FCSTD DOCUMENT  (FreeCAD 1.0R39109 (Git))
Label: sway_platform
License: All rights reserved
LicenseURL: https://en.wikipedia.org/wiki/All_rights_reserved
objects: App::Link×28, App::FeaturePython×28, Assembly::JointGroup×1, Assembly::AssemblyObject×1
EXTERNAL_REF file=../parts_library/SC25UU_to_SH25.FCStd obj=Body
EXTERNAL_REF file=../parts_library/SC25UU.FCStd obj=Part__Feature341
EXTERNAL_REF file=../parts_library/SH25.FCStd obj=Part__Feature337
EXTERNAL_REF file=../parts_library/linear_shaft.FCStd obj=Body001
EXTERNAL_REF file=../parts_library/DSG16H_to_SH25.FCStd obj=Body
EXTERNAL_REF file=../parts_library/SFU1605.FCStd obj=Part__Feature048
EXTERNAL_REF file=../parts_library/SFU1605.FCStd obj=Part__Feature047
EXTERNAL_REF file=../parts_library/motor.FCStd obj=SERVOMOTOR_80ST_M02430
EXTERNAL_REF file=../parts_library/coupler.FCStd obj=Body
EXTERNAL_REF file=../parts_library/SFU1605.FCStd obj=SFU1605_250_v6
EXTERNAL_REF file=../parts_library/SFU1605.FCStd obj=BK12_v3
EXTERNAL_REF file=sway_SC25UU_to_SH25_with_plate.FCStd obj=Body
EXTERNAL_REF file=sway_motor_mount_rear_plate.FCStd obj=Body
EXTERNAL_REF file=sway_motor_mount_front_plate.FCStd obj=Body
EXTERNAL_REF file=sway_motor_mount_front_plate_shaft_support.FCStd obj=Body
EXTERNAL_REF file=sway_motor_mount_side.FCStd obj=Body
EXTERNAL_REF file=sway_motor_mount_top.FCStd obj=Body
EXTERNAL_REF file=sway_motor_mount_bottom.FCStd obj=Body

FEATURE [App::Link] SC25UU_to_SH25  label="SC25UU_to_SH25_000"
  LinkedObject = -> <external ../parts_library/SC25UU_to_SH25.FCStd>#Body
FEATURE [App::Link] SC25UU_to_SH026  label="SC25UU_to_SH25_001"
  LinkPlacement = pos=(1e-15,204,-1e-16) rot=(0,0,1;0rad)
  LinkedObject = -> <external ../parts_library/SC25UU_to_SH25.FCStd>#Body
  Placement = pos=(1e-15,204,-1e-16) rot=(0,0,1;0rad)
FEATURE [App::FeaturePython] GroundedJoint  label="GroundedJoint_SC25UU_to_SH25_000"  # Assembly grounded joint (typed FeaturePython)
  ObjectToGround = -> SC25UU_to_SH25
FEATURE [App::FeaturePython] Joint  label="Fixed_SC25UU_to_SH25_001"  # Assembly joint (typed FeaturePython)
  Activated = true
  AngleMax = 0
  AngleMin = 0
  Detach1 = false
  Detach2 = false
  Distance = 0
  Distance2 = 0
  EnableAngleMax = false
  EnableAngleMin = false
  EnableLengthMax = false
  EnableLengthMin = false
  JointType = 0 (Fixed)
  LengthMax = 0
  LengthMin = 0
  Offset2 = pos=(0,0,-204) rot=(0,0,1;0rad)
  Placement1 = pos=(38,-1.5,5) rot=(-1,0,0;1.5708rad)
  Placement2 = pos=(38,-205.5,5) rot=(-1,0,0;1.5708rad)
  Reference1 = -> Assembly [SC25UU_to_SH25.Face9,SC25UU_to_SH25.Face9]
  Reference2 = -> Assembly [SC25UU_to_SH026.Face9,SC25UU_to_SH026.Face9]
FEATURE [App::Link] SC25UU  label="SC25UU_000"
  LinkPlacement = pos=(38,67,-415.5) rot=(1,0,0;1.5708rad)
  LinkedObject = -> <external ../parts_library/SC25UU.FCStd>#Part__Feature341
  Placement = pos=(38,67,-415.5) rot=(1,0,0;1.5708rad)
FEATURE [App::Link] SC25UU001  label="SC25UU_001"
  LinkPlacement = pos=(38,271,-415.5) rot=(1,0,0;1.5708rad)
  LinkedObject = -> <external ../parts_library/SC25UU.FCStd>#Part__Feature341
  Placement = pos=(38,271,-415.5) rot=(1,0,0;1.5708rad)
FEATURE [App::Link] SC25UU002  label="SC25UU_002"
  LinkPlacement = pos=(442,67,-415.5) rot=(1,0,0;1.5708rad)
  LinkedObject = -> <external ../parts_library/SC25UU.FCStd>#Part__Feature341
  Placement = pos=(442,67,-415.5) rot=(1,0,0;1.5708rad)
FEATURE [App::Link] SC25UU003  label="SC25UU_003"
  LinkPlacement = pos=(442,271,-415.5) rot=(1,0,0;1.5708rad)
  LinkedObject = -> <external ../parts_library/SC25UU.FCStd>#Part__Feature341
  Placement = pos=(442,271,-415.5) rot=(1,0,0;1.5708rad)
FEATURE [App::FeaturePython] Joint003  label="Fixed_SC25UU_000"  # Assembly joint (typed FeaturePython)
  Activated = true
  AngleMax = 0
  AngleMin = 0
  Detach1 = false
  Detach2 = false
  Distance = 0
  Distance2 = 0
  EnableAngleMax = false
  EnableAngleMin = false
  EnableLengthMax = false
  EnableLengthMin = false
  JointType = 0 (Fixed)
  LengthMax = 0
  LengthMin = 0
  Offset2 = pos=(0,0,0) rot=(0,0,-1;1.5708rad)
  Placement1 = pos=(-27,415.5,58.5) rot=(0.57735,-0.57735,0.57735;2.0944rad)
  Placement2 = pos=(11,8.5,0) rot=(0,0,-1;1.5708rad)
  Reference1 = -> Assembly [SC25UU.Edge66,SC25UU.Edge66]
  Reference2 = -> Assembly [SC25UU_to_SH25.Edge16,SC25UU_to_SH25.Edge16]
FEATURE [App::FeaturePython] Joint004  label="Fixed_SC25UU_001"  # Assembly joint (typed FeaturePython)
  Activated = true
  AngleMax = 0
  AngleMin = 0
  Detach1 = false
  Detach2 = false
  Distance = 0
  Distance2 = 0
  EnableAngleMax = false
  EnableAngleMin = false
  EnableLengthMax = false
  EnableLengthMin = false
  JointType = 0 (Fixed)
  LengthMax = 0
  LengthMin = 0
  Offset2 = pos=(0,0,0) rot=(0,0,-1;1.5708rad)
  Placement1 = pos=(11,8.5,0) rot=(0,0,1;0rad)
  Placement2 = pos=(-27,415.5,58.5) rot=(1,0,0;1.5708rad)
  Reference1 = -> Assembly [SC25UU_to_SH026.Edge16,SC25UU_to_SH026.Edge16]
  Reference2 = -> Assembly [SC25UU001.Edge66,SC25UU001.Edge66]
FEATURE [App::Link] SH25  label="SH25_000"
  LinkPlacement = pos=(-901.062,343.027,-226.938) rot=(0,0,1;0rad)
  LinkedObject = -> <external ../parts_library/SH25.FCStd>#Part__Feature337
  Placement = pos=(-901.062,343.027,-226.938) rot=(0,0,1;0rad)
FEATURE [App::Link] SH026  label="SH25_001"
  LinkPlacement = pos=(977.062,-72.0272,-226.938) rot=(0,0,1;3.14159rad)
  LinkedObject = -> <external ../parts_library/SH25.FCStd>#Part__Feature337
  Placement = pos=(977.062,-72.0272,-226.938) rot=(0,0,1;3.14159rad)
FEATURE [App::Link] SH027  label="SH25_002"
  LinkPlacement = pos=(-497.062,343.027,-226.938) rot=(0,0,1;0rad)
  LinkedObject = -> <external ../parts_library/SH25.FCStd>#Part__Feature337
  Placement = pos=(-497.062,343.027,-226.938) rot=(0,0,1;0rad)
FEATURE [App::Link] SH028  label="SH25_003"
  LinkPlacement = pos=(1381.06,-72.0272,-226.938) rot=(0,0,1;3.14159rad)
  LinkedObject = -> <external ../parts_library/SH25.FCStd>#Part__Feature337
  Placement = pos=(1381.06,-72.0272,-226.938) rot=(0,0,1;3.14159rad)
FEATURE [App::FeaturePython] Joint007  label="Fixed_SH25_000"  # Assembly joint (typed FeaturePython)
  Activated = true
  AngleMax = 0
  AngleMin = 0
  Detach1 = false
  Detach2 = false
  Distance = 0
  Distance2 = 0
  EnableAngleMax = false
  EnableAngleMin = false
  EnableLengthMax = false
  EnableLengthMin = false
  JointType = 0 (Fixed)
  LengthMax = 0
  LengthMin = 0
  Offset2 = pos=(0,0,0) rot=(0,0,1;3.14159rad)
  Placement1 = pos=(38,5.5,10) rot=(0,0,1;0rad)
  Placement2 = pos=(939.062,-337.527,236.938) rot=(0,0,1;0rad)
  Reference1 = -> Assembly [SC25UU_to_SH25.Edge46,SC25UU_to_SH25.Edge46]
  Reference2 = -> Assembly [SH25.Edge16,SH25.Edge16]
FEATURE [App::FeaturePython] Joint008  label="Fixed_SH25_001"  # Assembly joint (typed FeaturePython)
  Activated = true
  AngleMax = 0
  AngleMin = 0
  Detach1 = false
  Detach2 = false
  Distance = 0
  Distance2 = 0
  EnableAngleMax = false
  EnableAngleMin = false
  EnableLengthMax = false
  EnableLengthMin = false
  JointType = 0 (Fixed)
  LengthMax = 0
  LengthMin = 0
  Placement1 = pos=(939.062,-337.527,236.938) rot=(0,0,-1;3.14159rad)
  Placement2 = pos=(38,61.5,10) rot=(0,0,1;0rad)
  Reference1 = -> Assembly [SH026.Edge16,SH026.Edge16]
  Reference2 = -> Assembly [SC25UU_to_SH026.Edge49,SC25UU_to_SH026.Edge49]
FEATURE [App::Link] linear_shaft_25x428  label="linear_shaft_25x428_front"
  LinkPlacement = pos=(454,33.5,45) rot=(0,0,-1;1.5708rad)
  LinkedObject = -> <external ../parts_library/linear_shaft.FCStd>#Body001
  Placement = pos=(454,33.5,45) rot=(0,0,-1;1.5708rad)
FEATURE [App::Link] linear_shaft_25x429  label="linear_shaft_25x428_rear"
  LinkPlacement = pos=(454,237.5,45) rot=(0.707107,0.707107,0;3.14159rad)
  LinkedObject = -> <external ../parts_library/linear_shaft.FCStd>#Body001
  Placement = pos=(454,237.5,45) rot=(0.707107,0.707107,0;3.14159rad)
FEATURE [App::FeaturePython] Joint011  label="Fixed_linear_shaft_25x428_front"  # Assembly joint (typed FeaturePython)
  Activated = true
  AngleMax = 0
  AngleMin = 0
  Detach1 = false
  Detach2 = false
  Distance = 0
  Distance2 = 0
  EnableAngleMax = false
  EnableAngleMin = false
  EnableLengthMax = false
  EnableLengthMin = false
  JointType = 0 (Fixed)
  LengthMax = 0
  LengthMin = 0
  Placement1 = pos=(-7.1e-15,-428,-1.421e-13) rot=(-1,0,0;4.71239rad)
  Placement2 = pos=(927.062,-309.527,271.938) rot=(-0.57735,0.57735,-0.57735;2.0944rad)
  Reference1 = -> Assembly [linear_shaft_25x428.Edge3,linear_shaft_25x428.Edge3]
  Reference2 = -> Assembly [SH25.Edge18,SH25.Edge18]
FEATURE [App::FeaturePython] Joint012  label="Fixed_linear_shaft_25x428_rear"  # Assembly joint (typed FeaturePython)
  Activated = true
  AngleMax = 0
  AngleMin = 0
  Detach1 = false
  Detach2 = false
  Distance = 0
  Distance2 = 0
  EnableAngleMax = false
  EnableAngleMin = false
  EnableLengthMax = false
  EnableLengthMin = false
  JointType = 0 (Fixed)
  LengthMax = 0
  LengthMin = 0
  Placement1 = pos=(0,-428,-1.137e-13) rot=(-1,0,0;4.71239rad)
  Placement2 = pos=(951.062,-309.527,271.938) rot=(-0.57735,0.57735,-0.57735;2.0944rad)
  Reference1 = -> Assembly [linear_shaft_25x429.Edge3,linear_shaft_25x429.Edge3]
  Reference2 = -> Assembly [SH026.Edge26,SH026.Edge26]
FEATURE [App::Link] SH029  label="SH25_004"
  LinkPlacement = pos=(1179.06,-72.0272,-226.938) rot=(0,0,1;3.14159rad)
  LinkedObject = -> <external ../parts_library/SH25.FCStd>#Part__Feature337
  Placement = pos=(1179.06,-72.0272,-226.938) rot=(0,0,1;3.14159rad)
FEATURE [App::FeaturePython] Joint013  label="Fixed_SH25_004"  # Assembly joint (typed FeaturePython)
  Activated = true
  AngleMax = 0
  AngleMin = 0
  Detach1 = false
  Detach2 = false
  Distance = 0
  Distance2 = 0
  EnableAngleMax = false
  EnableAngleMin = false
  EnableLengthMax = false
  EnableLengthMin = false
  JointType = 0 (Fixed)
  LengthMax = 0
  LengthMin = 0
  Offset2 = pos=(0,0,202) rot=(0,0,1;0rad)
  Placement1 = pos=(0,-428,-1.137e-13) rot=(-1,0,0;4.71239rad)
  Placement2 = pos=(1153.06,-309.527,271.938) rot=(-0.57735,0.57735,-0.57735;2.0944rad)
  Reference1 = -> Assembly [linear_shaft_25x429.Edge3,linear_shaft_25x429.Edge3]
  Reference2 = -> Assembly [SH029.Edge26,SH029.Edge26]
FEATURE [App::Link] DSG16H_to_SH25
  LinkPlacement = pos=(215,218.5,-2) rot=(0,0,1;0rad)
  LinkedObject = -> <external ../parts_library/DSG16H_to_SH25.FCStd>#Body
  Placement = pos=(215,218.5,-2) rot=(0,0,1;0rad)
FEATURE [App::FeaturePython] Joint014  label="Fixed_DSG16H_to_SH25"  # Assembly joint (typed FeaturePython)
  Activated = true
  AngleMax = 0
  AngleMin = 0
  Detach1 = false
  Detach2 = false
  Distance = 0
  Distance2 = 0
  EnableAngleMax = false
  EnableAngleMin = false
  EnableLengthMax = false
  EnableLengthMin = false
  JointType = 0 (Fixed)
  LengthMax = 0
  LengthMin = 0
  Placement1 = pos=(25,-9,12) rot=(0,0,1;0rad)
  Placement2 = pos=(939.062,-281.527,236.938) rot=(0,0,-1;3.14159rad)
  Reference1 = -> Assembly [DSG16H_to_SH25.Edge103,DSG16H_to_SH25.Edge103]
  Reference2 = -> Assembly [SH029.Edge8,SH029.Edge8]
FEATURE [App::Link] DSG16H
  LinkPlacement = pos=(240,217.5,-22) rot=(0,0,1;0rad)
  LinkedObject = -> <external ../parts_library/SFU1605.FCStd>#Part__Feature048
  Placement = pos=(240,217.5,-22) rot=(0,0,1;0rad)
FEATURE [App::FeaturePython] Joint015  label="Fixed_DSG16H"  # Assembly joint (typed FeaturePython)
  Activated = true
  AngleMax = 0
  AngleMin = 0
  Detach1 = false
  Detach2 = false
  Distance = 0
  Distance2 = 0
  EnableAngleMax = false
  EnableAngleMin = false
  EnableLengthMax = false
  EnableLengthMin = false
  JointType = 0 (Fixed)
  LengthMax = 0
  LengthMin = 0
  Offset2 = pos=(0,0,0) rot=(0,0,1;3.14159rad)
  Placement1 = pos=(-20,8,20) rot=(0,0,1;3.14159rad)
  Placement2 = pos=(5,7,0) rot=(0,0,1;3.14159rad)
  Reference1 = -> Assembly [DSG16H.Edge1307,DSG16H.Edge1307]
  Reference2 = -> Assembly [DSG16H_to_SH25.Edge20,DSG16H_to_SH25.Edge20]
FEATURE [App::Link] SFU1605_ball_screw_nut
  LinkPlacement = pos=(240,207.25,-22) rot=(0,-1,0;1.5708rad)
  LinkedObject = -> <external ../parts_library/SFU1605.FCStd>#Part__Feature047
  Placement = pos=(240,207.25,-22) rot=(0,-1,0;1.5708rad)
FEATURE [App::FeaturePython] Joint016  label="Fixed_SFU1605_ball_screw_nut"  # Assembly joint (typed FeaturePython)
  Activated = true
  AngleMax = 0
  AngleMin = 0
  Detach1 = false
  Detach2 = false
  Distance = 0
  Distance2 = 0
  EnableAngleMax = false
  EnableAngleMin = false
  EnableLengthMax = false
  EnableLengthMin = false
  JointType = 0 (Fixed)
  LengthMax = 0
  LengthMin = 0
  Placement1 = pos=(0,20,0) rot=(-1,0,0;1.5708rad)
  Placement2 = pos=(7.1e-15,30.25,0) rot=(0.57735,0.57735,-0.57735;2.0944rad)
  Reference1 = -> Assembly [DSG16H.Face478,DSG16H.Face478]
  Reference2 = -> Assembly [SFU1605_ball_screw_nut.Face46,SFU1605_ball_screw_nut.Face46]
FEATURE [App::Link] _0ST_M02438  label="80ST-M02438"
  LinkPlacement = pos=(342.4,135.5,30) rot=(0.57735,-0.57735,-0.57735;2.0944rad)
  LinkedObject = -> <external ../parts_library/motor.FCStd>#SERVOMOTOR_80ST_M02430
  Placement = pos=(342.4,135.5,30) rot=(0.57735,-0.57735,-0.57735;2.0944rad)
FEATURE [App::FeaturePython] Joint017  label="Fixed_80ST-M02438"  # Assembly joint (typed FeaturePython)
  Activated = true
  AngleMax = 0
  AngleMin = 0
  Detach1 = false
  Detach2 = false
  Distance = 0
  Distance2 = 0
  EnableAngleMax = false
  EnableAngleMin = false
  EnableLengthMax = false
  EnableLengthMin = false
  JointType = 0 (Fixed)
  LengthMax = 0
  LengthMin = 0
  Offset1 = pos=(-102,15,0) rot=(0,0,1;0rad)
  Offset2 = pos=(0,0,-31) rot=(0,0,1;0rad)
  Placement1 = pos=(-102,3e-15,15) rot=(-1,0,0;4.71239rad)
  Placement2 = pos=(0,0,-111.6) rot=(0,1,0;3.14159rad)
  Reference1 = -> Assembly [linear_shaft_25x429.Edge2,linear_shaft_25x429.Edge2]
  Reference2 = -> Assembly [_0ST_M02438.Part__Feature004.Edge14,_0ST_M02438.Part__Feature004.Edge14]
FEATURE [App::Link] coupler_10x19
  LinkPlacement = pos=(266.25,135.5,30) rot=(-0.57735,0.57735,0.57735;2.0944rad)
  LinkedObject = -> <external ../parts_library/coupler.FCStd>#Body
  Placement = pos=(266.25,135.5,30) rot=(-0.57735,0.57735,0.57735;2.0944rad)
FEATURE [App::FeaturePython] Joint018  label="Fixed_coupler_10x19"  # Assembly joint (typed FeaturePython)
  Activated = true
  AngleMax = 0
  AngleMin = 0
  Detach1 = false
  Detach2 = false
  Distance = 0
  Distance2 = 0
  EnableAngleMax = false
  EnableAngleMin = false
  EnableLengthMax = false
  EnableLengthMin = false
  JointType = 0 (Fixed)
  LengthMax = 0
  LengthMin = 0
  Offset2 = pos=(0,0,1.65) rot=(0,0,1;0rad)
  Placement1 = pos=(0,0,43) rot=(0,0,1;0rad)
  Placement2 = pos=(3.7e-15,-33.15,-7e-16) rot=(1,0,0;1.5708rad)
  Reference1 = -> Assembly [_0ST_M02438.Part__Feature002.Edge5,_0ST_M02438.Part__Feature002.Edge5]
  Reference2 = -> Assembly [coupler_10x19.Edge9,coupler_10x19.Edge9]
FEATURE [App::Link] SFU1605_ball_screw_250mm
  LinkPlacement = pos=(497.25,135.5,30) rot=(0.57735,0.57735,0.57735;2.0944rad)
  LinkedObject = -> <external ../parts_library/SFU1605.FCStd>#SFU1605_250_v6
  Placement = pos=(497.25,135.5,30) rot=(0.57735,0.57735,0.57735;2.0944rad)
FEATURE [App::FeaturePython] Joint019  label="Fixed_SFU1605_ball_screw_250mm"  # Assembly joint (typed FeaturePython)
  Activated = true
  AngleMax = 0
  AngleMin = 0
  Detach1 = false
  Detach2 = false
  Distance = 0
  Distance2 = 0
  EnableAngleMax = false
  EnableAngleMin = false
  EnableLengthMax = false
  EnableLengthMin = false
  JointType = 0 (Fixed)
  LengthMax = 0
  LengthMin = 0
  Offset2 = pos=(0,0,4) rot=(0,0,1;0rad)
  Placement1 = pos=(2e-16,3e-16,0) rot=(0,0,1;0rad)
  Placement2 = pos=(3.1e-15,-14.5,1.8e-15) rot=(-1,0,0;1.5708rad)
  Reference1 = -> Assembly [SFU1605_ball_screw_250mm.Part__Feature110.Edge105,SFU1605_ball_screw_250mm.Part__Feature110.Edge105]
  Reference2 = -> Assembly [coupler_10x19.Edge7,coupler_10x19.Edge7]
FEATURE [App::Link] BK12
  LinkPlacement = pos=(240,135.5,55) rot=(0.707107,-0.707107,0;3.14159rad)
  LinkedObject = -> <external ../parts_library/SFU1605.FCStd>#BK12_v3
  Placement = pos=(240,135.5,55) rot=(0.707107,-0.707107,0;3.14159rad)
FEATURE [App::FeaturePython] Joint020  label="Fixed_BK12"  # Assembly joint (typed FeaturePython)
  Activated = true
  AngleMax = 0
  AngleMin = 0
  Detach1 = false
  Detach2 = false
  Distance = 0
  Distance2 = 0
  EnableAngleMax = false
  EnableAngleMin = false
  EnableLengthMax = false
  EnableLengthMin = false
  JointType = 0 (Fixed)
  LengthMax = 0
  LengthMin = 0
  Placement1 = pos=(2e-16,3e-16,-53.75) rot=(0,0,1;0rad)
  Placement2 = pos=(1.1e-15,13,25) rot=(0,0.707107,0.707107;3.14159rad)
  Reference1 = -> Assembly [SFU1605_ball_screw_250mm.Part__Feature110.Edge52,SFU1605_ball_screw_250mm.Part__Feature110.Edge52]
  Reference2 = -> Assembly [BK12.Part__Feature030.Edge19,BK12.Part__Feature030.Edge19]
FEATURE [App::Link] sway_SC25UU_to_SH25_with_plate  label="sway_SC25UU_to_SH25_with_plate_001"
  LinkPlacement = pos=(404,204,3e-16) rot=(0,0,1;0rad)
  LinkedObject = -> <external sway_SC25UU_to_SH25_with_plate.FCStd>#Body
  Placement = pos=(404,204,3e-16) rot=(0,0,1;0rad)
FEATURE [App::FeaturePython] Joint022  label="Fixed_SC25UU_003"  # Assembly joint (typed FeaturePython)
  Activated = true
  AngleMax = 0
  AngleMin = 0
  Detach1 = false
  Detach2 = false
  Distance = 0
  Distance2 = 0
  EnableAngleMax = false
  EnableAngleMin = false
  EnableLengthMax = false
  EnableLengthMin = false
  JointType = 0 (Fixed)
  LengthMax = 0
  LengthMin = 0
  Offset2 = pos=(0,0,0) rot=(0,0,-1;1.5708rad)
  Placement1 = pos=(65,58.5,0) rot=(0,0,1;0rad)
  Placement2 = pos=(27,415.5,8.5) rot=(1,0,0;1.5708rad)
  Reference1 = -> Assembly [sway_SC25UU_to_SH25_with_plate.Edge31,sway_SC25UU_to_SH25_with_plate.Edge31]
  Reference2 = -> Assembly [SC25UU003.Edge29,SC25UU003.Edge29]
FEATURE [App::FeaturePython] Joint023  label="Fixed_SH25_003"  # Assembly joint (typed FeaturePython)
  Activated = true
  AngleMax = 0
  AngleMin = 0
  Detach1 = false
  Detach2 = false
  Distance = 0
  Distance2 = 0
  EnableAngleMax = false
  EnableAngleMin = false
  EnableLengthMax = false
  EnableLengthMin = false
  JointType = 0 (Fixed)
  LengthMax = 0
  LengthMin = 0
  Placement1 = pos=(38,61.5,10) rot=(0,0,1;0rad)
  Placement2 = pos=(939.062,-337.527,236.938) rot=(0,0,-1;3.14159rad)
  Reference1 = -> Assembly [sway_SC25UU_to_SH25_with_plate.Edge90,sway_SC25UU_to_SH25_with_plate.Edge90]
  Reference2 = -> Assembly [SH028.Edge16,SH028.Edge16]
FEATURE [App::Link] sway_motor_mount_rear_plate
  LinkPlacement = pos=(430,272.5,5) rot=(0,0,1;3.14159rad)
  LinkedObject = -> <external sway_motor_mount_rear_plate.FCStd>#Body
  Placement = pos=(430,272.5,5) rot=(0,0,1;3.14159rad)
FEATURE [App::FeaturePython] Joint024  label="Fixed_sway_motor_mount_rear_plate"  # Assembly joint (typed FeaturePython)
  Activated = true
  AngleMax = 0
  AngleMin = 0
  Detach1 = false
  Detach2 = false
  Distance = 0
  Distance2 = 0
  EnableAngleMax = false
  EnableAngleMin = false
  EnableLengthMax = false
  EnableLengthMin = false
  JointType = 0 (Fixed)
  LengthMax = 0
  LengthMin = 0
  Offset2 = pos=(0,0,0) rot=(0,0,1;3.14159rad)
  Placement1 = pos=(11,58.5,5) rot=(1,0,0;3.14159rad)
  Placement2 = pos=(15,10,0) rot=(0,0,1;3.14159rad)
  Reference1 = -> Assembly [sway_SC25UU_to_SH25_with_plate.Edge39,sway_SC25UU_to_SH25_with_plate.Edge39]
  Reference2 = -> Assembly [sway_motor_mount_rear_plate.Edge10,sway_motor_mount_rear_plate.Edge10]
FEATURE [App::Link] sway_SC25UU_to_SH25_with_plate001  label="sway_SC25UU_to_SH25_with_plate_000"
  LinkPlacement = pos=(404,-1e-16,3e-16) rot=(0,0,1;0rad)
  LinkedObject = -> <external sway_SC25UU_to_SH25_with_plate.FCStd>#Body
  Placement = pos=(404,-1e-16,3e-16) rot=(0,0,1;0rad)
FEATURE [App::FeaturePython] Joint025  label="Fixed_sway_SC25UU_to_SH25_with_plate_000"  # Assembly joint (typed FeaturePython)
  Activated = true
  AngleMax = 0
  AngleMin = 0
  Detach1 = false
  Detach2 = false
  Distance = 0
  Distance2 = 0
  EnableAngleMax = false
  EnableAngleMin = false
  EnableLengthMax = false
  EnableLengthMin = false
  JointType = 0 (Fixed)
  LengthMax = 0
  LengthMin = 0
  Offset1 = pos=(-404,0,0) rot=(0,0,1;0rad)
  Placement1 = pos=(-366,-1.5,5) rot=(-1,0,0;1.5708rad)
  Placement2 = pos=(38,-1.5,5) rot=(-1,0,0;1.5708rad)
  Reference1 = -> Assembly [sway_SC25UU_to_SH25_with_plate001.Face9,sway_SC25UU_to_SH25_with_plate001.Face9]
  Reference2 = -> Assembly [SC25UU_to_SH25.Face9,SC25UU_to_SH25.Face9]
FEATURE [App::FeaturePython] Joint026  label="Fixed_sway_SC25UU_to_SH25_with_plate_001"  # Assembly joint (typed FeaturePython)
  Activated = true
  AngleMax = 0
  AngleMin = 0
  Detach1 = false
  Detach2 = false
  Distance = 0
  Distance2 = 0
  EnableAngleMax = false
  EnableAngleMin = false
  EnableLengthMax = false
  EnableLengthMin = false
  JointType = 0 (Fixed)
  LengthMax = 0
  LengthMin = 0
  Offset2 = pos=(0,0,-204) rot=(0,0,1;0rad)
  Placement1 = pos=(38,-1.5,5) rot=(-1,0,0;1.5708rad)
  Placement2 = pos=(38,-205.5,5) rot=(-1,0,0;1.5708rad)
  Reference1 = -> Assembly [sway_SC25UU_to_SH25_with_plate001.Face9,sway_SC25UU_to_SH25_with_plate001.Face9]
  Reference2 = -> Assembly [sway_SC25UU_to_SH25_with_plate.Face9,sway_SC25UU_to_SH25_with_plate.Face9]
FEATURE [App::FeaturePython] Joint027  label="Fixed_SC25UU_002"  # Assembly joint (typed FeaturePython)
  Activated = true
  AngleMax = 0
  AngleMin = 0
  Detach1 = false
  Detach2 = false
  Distance = 0
  Distance2 = 0
  EnableAngleMax = false
  EnableAngleMin = false
  EnableLengthMax = false
  EnableLengthMin = false
  JointType = 0 (Fixed)
  LengthMax = 0
  LengthMin = 0
  Offset2 = pos=(0,0,0) rot=(0,0,-1;1.5708rad)
  Placement1 = pos=(27,415.5,8.5) rot=(0.57735,-0.57735,0.57735;2.0944rad)
  Placement2 = pos=(65,58.5,0) rot=(0,0,-1;1.5708rad)
  Reference1 = -> Assembly [SC25UU002.Edge29,SC25UU002.Edge29]
  Reference2 = -> Assembly [sway_SC25UU_to_SH25_with_plate001.Edge31,sway_SC25UU_to_SH25_with_plate001.Edge31]
FEATURE [App::FeaturePython] Joint028  label="Fixed_SH25_002"  # Assembly joint (typed FeaturePython)
  Activated = true
  AngleMax = 0
  AngleMin = 0
  Detach1 = false
  Detach2 = false
  Distance = 0
  Distance2 = 0
  EnableAngleMax = false
  EnableAngleMin = false
  EnableLengthMax = false
  EnableLengthMin = false
  JointType = 0 (Fixed)
  LengthMax = 0
  LengthMin = 0
  Offset2 = pos=(0,0,0) rot=(0,0,1;3.14159rad)
  Placement1 = pos=(38,61.5,10) rot=(0,0,1;0rad)
  Placement2 = pos=(939.062,-281.527,236.938) rot=(0,0,1;0rad)
  Reference1 = -> Assembly [sway_SC25UU_to_SH25_with_plate001.Edge90,sway_SC25UU_to_SH25_with_plate001.Edge90]
  Reference2 = -> Assembly [SH027.Edge8,SH027.Edge8]
FEATURE [App::Link] sway_motor_mount_front_plate
  LinkPlacement = pos=(430,68.5,5) rot=(0,0,1;3.14159rad)
  LinkedObject = -> <external sway_motor_mount_front_plate.FCStd>#Body
  Placement = pos=(430,68.5,5) rot=(0,0,1;3.14159rad)
FEATURE [App::FeaturePython] Joint029  label="Fixed_sway_motor_mount_front_plate"  # Assembly joint (typed FeaturePython)
  Activated = true
  AngleMax = 0
  AngleMin = 0
  Detach1 = false
  Detach2 = false
  Distance = 0
  Distance2 = 0
  EnableAngleMax = false
  EnableAngleMin = false
  EnableLengthMax = false
  EnableLengthMin = false
  JointType = 0 (Fixed)
  LengthMax = 0
  LengthMin = 0
  Offset2 = pos=(0,0,0) rot=(0,0,1;3.14159rad)
  Placement1 = pos=(11,58.5,5) rot=(1,0,0;3.14159rad)
  Placement2 = pos=(15,10,0) rot=(0,0,1;3.14159rad)
  Reference1 = -> Assembly [sway_SC25UU_to_SH25_with_plate001.Edge39,sway_SC25UU_to_SH25_with_plate001.Edge39]
  Reference2 = -> Assembly [sway_motor_mount_front_plate.Edge14,sway_motor_mount_front_plate.Edge14]
FEATURE [App::Link] sway_motor_mount_front_plate_shaft_support
  LinkPlacement = pos=(252,33.5,45) rot=(0,0,1;3.14159rad)
  LinkedObject = -> <external sway_motor_mount_front_plate_shaft_support.FCStd>#Body
  Placement = pos=(252,33.5,45) rot=(0,0,1;3.14159rad)
FEATURE [App::FeaturePython] Joint030  label="Fixed_sway_motor_mount_front_plate_shaft_support"  # Assembly joint (typed FeaturePython)
  Activated = true
  AngleMax = 0
  AngleMin = 0
  Detach1 = false
  Detach2 = false
  Distance = 0
  Distance2 = 0
  EnableAngleMax = false
  EnableAngleMin = false
  EnableLengthMax = false
  EnableLengthMin = false
  JointType = 0 (Fixed)
  LengthMax = 0
  LengthMin = 0
  Offset2 = pos=(0,0,-202) rot=(0,0,1;0rad)
  Placement1 = pos=(951.062,-309.527,271.938) rot=(-0.57735,0.57735,-0.57735;2.0944rad)
  Placement2 = pos=(-202,-2.018e-13,-2.018e-13) rot=(-0.57735,-0.57735,-0.57735;4.18879rad)
  Reference1 = -> Assembly [SH027.Edge26,SH027.Edge26]
  Reference2 = -> Assembly [sway_motor_mount_front_plate_shaft_support.Edge26,sway_motor_mount_front_plate_shaft_support.Edge26]
FEATURE [App::Link] sway_motor_mount_side
  LinkPlacement = pos=(334.4,135.565,9.95) rot=(0,0,-1;1.5708rad)
  LinkedObject = -> <external sway_motor_mount_side.FCStd>#Body
  Placement = pos=(334.4,135.565,9.95) rot=(0,0,-1;1.5708rad)
FEATURE [App::Link] sway_motor_mount_top
  LinkPlacement = pos=(434,135.5,10) rot=(0,0,1;1.5708rad)
  LinkedObject = -> <external sway_motor_mount_top.FCStd>#Body
  Placement = pos=(434,135.5,10) rot=(0,0,1;1.5708rad)
FEATURE [App::FeaturePython] Joint032  label="Fixed_sway_motor_mount_top"  # Assembly joint (typed FeaturePython)
  Activated = true
  AngleMax = 0
  AngleMin = 0
  Detach1 = false
  Detach2 = false
  Distance = 0
  Distance2 = 0
  EnableAngleMax = false
  EnableAngleMin = false
  EnableLengthMax = false
  EnableLengthMin = false
  JointType = 0 (Fixed)
  LengthMax = 0
  LengthMin = 0
  Offset1 = pos=(0,-0.4,0) rot=(0,0,1;0rad)
  Offset2 = pos=(0,0,0) rot=(0,0,1;1.5708rad)
  Placement1 = pos=(1.95e-14,40.4,-106.6) rot=(-0.707107,0,0.707107;3.14159rad)
  Placement2 = pos=(0,-15,60.4) rot=(0.57735,-0.57735,0.57735;4.18879rad)
  Reference1 = -> Assembly [_0ST_M02438.Part__Feature006.Edge472,_0ST_M02438.Part__Feature006.Edge472]
  Reference2 = -> Assembly [sway_motor_mount_top.Edge23,sway_motor_mount_top.Edge23]
FEATURE [App::Link] sway_motor_mount_bottom
  LinkPlacement = pos=(419,135.5,10) rot=(0,0,-1;1.5708rad)
  LinkedObject = -> <external sway_motor_mount_bottom.FCStd>#Body
  Placement = pos=(419,135.5,10) rot=(0,0,-1;1.5708rad)
FEATURE [App::FeaturePython] Joint033  label="Fixed_sway_motor_mount_bottom"  # Assembly joint (typed FeaturePython)
  Activated = true
  AngleMax = 0
  AngleMin = 0
  Detach1 = false
  Detach2 = false
  Distance = 0
  Distance2 = 0
  EnableAngleMax = false
  EnableAngleMin = false
  EnableLengthMax = false
  EnableLengthMin = false
  JointType = 0 (Fixed)
  LengthMax = 0
  LengthMin = 0
  Offset1 = pos=(0.4,-30,0) rot=(0,0,1;0rad)
  Offset2 = pos=(0,0,0) rot=(0,0,-1;1.5708rad)
  Placement1 = pos=(0,30,-20) rot=(0.707107,0,0.707107;3.14159rad)
  Placement2 = pos=(2.629e-13,-40,-106.6) rot=(0.57735,0.57735,0.57735;2.0944rad)
  Reference1 = -> Assembly [sway_motor_mount_bottom.Edge11,sway_motor_mount_bottom.Edge11]
  Reference2 = -> Assembly [_0ST_M02438.Part__Feature006.Edge167,_0ST_M02438.Part__Feature006.Edge167]
FEATURE [App::FeaturePython] Joint034  label="Fixed_sway_motor_mount_side"  # Assembly joint (typed FeaturePython)
  Activated = true
  AngleMax = 0
  AngleMin = 0
  Detach1 = false
  Detach2 = false
  Distance = 0
  Distance2 = 0
  EnableAngleMax = false
  EnableAngleMin = false
  EnableLengthMax = false
  EnableLengthMin = false
  JointType = 0 (Fixed)
  LengthMax = 0
  LengthMin = 0
  Placement1 = pos=(-31.75,0,51.75) rot=(1,0,0;1.5708rad)
  Placement2 = pos=(-31.815,31.7,8) rot=(0,0,1;0rad)
  Reference1 = -> Assembly [sway_motor_mount_side.Edge399,sway_motor_mount_side.Edge399]
  Reference2 = -> Assembly [_0ST_M02438.Part__Feature003.Edge20,_0ST_M02438.Part__Feature003.Edge20]
FEATURE [Assembly::JointGroup] Joints
  Group = -> [GroundedJoint,Joint,Joint003,Joint004,Joint007,Joint008,Joint011,Joint012,Joint013,Joint014,Joint015,Joint016,Joint017,Joint018,Joint019,Joint020,Joint022,Joint023,Joint024,Joint025,Joint026,Joint027,Joint028,Joint029,Joint030,Joint032,Joint033,Joint034]
FEATURE [Assembly::AssemblyObject] Assembly  label="sway_platform"
  Group = -> [Joints,SC25UU_to_SH25,SC25UU_to_SH026,GroundedJoint,Joint,SC25UU,SC25UU001,SC25UU002,SC25UU003,Joint003,Joint004,SH25,SH026,SH027,SH028,Joint007,Joint008,linear_shaft_25x428,linear_shaft_25x429,Joint011,Joint012,SH029,Joint013,DSG16H_to_SH25,Joint014,DSG16H,Joint015,SFU1605_ball_screw_nut,Joint016,_0ST_M02438,Joint017,coupler_10x19,Joint018,SFU1605_ball_screw_250mm,Joint019,BK12,Joint020,+20 more]
  Origin = -> Origin
  Type = Assembly

RESOLVED EXTERNAL PARTS (link-assembly join: the EXTERNAL_REF files above that resolve inside this repo's crawl, each included once):
---- part ../parts_library/DSG16H_to_SH25.FCStd = doc fcstd_5aafb13caf16 ----
FCSTD DOCUMENT  (FreeCAD 1.0R39109 (Git))
Label: DSG16H_to_SH25
License: All rights reserved
LicenseURL: https://en.wikipedia.org/wiki/All_rights_reserved
objects: Sketcher::SketchObject×4, PartDesign::Pocket×3, PartDesign::Pad×1, PartDesign::Fillet×1, PartDesign::Body×1
note: 24 computed .brp shape members not serialized (recipe doc carries the construction recipe); baked Part::Feature solids carry a one-line shape summary decoded from their .brp

FEATURE [Sketcher::SketchObject] Sketch
  ArcFitTolerance = 1e-06
  AttachmentSupport = -> [XY_Plane]
  FullyConstrained = true
  MakeInternals = false
  MapMode = 5
  sketch-geometry (19):
    g0: LineSegment StartX=50 StartY=0 StartZ=0 EndX=50 EndY=38 EndZ=0
    g1: LineSegment StartX=0 StartY=38 StartZ=0 EndX=0 EndY=0 EndZ=0
    g2: LineSegment [constr] StartX=5 StartY=7 StartZ=0 EndX=45 EndY=7 EndZ=0
    g3: LineSegment [constr] StartX=45 StartY=7 StartZ=0 EndX=45 EndY=31 EndZ=0
    g4: LineSegment [constr] StartX=45 StartY=31 StartZ=0 EndX=5 EndY=31 EndZ=0
    g5: LineSegment [constr] StartX=5 StartY=31 StartZ=0 EndX=5 EndY=7 EndZ=0
    g6: LineSegment [constr] StartX=0 StartY=0 StartZ=0 EndX=5 EndY=7 EndZ=0
    g7: LineSegment [constr] StartX=5 StartY=31 StartZ=0 EndX=-9e-16 EndY=38 EndZ=0
    g8: LineSegment [constr] StartX=45 StartY=31 StartZ=0 EndX=50 EndY=38 EndZ=0
    g9: Circle CenterX=5 CenterY=31 CenterZ=0 NormalX=0 NormalY=0 NormalZ=1 AngleXU=0 Radius=2.8
    g10: Circle CenterX=45 CenterY=31 CenterZ=0 NormalX=0 NormalY=0 NormalZ=1 AngleXU=0 Radius=2.8
    g11: Circle CenterX=45 CenterY=7 CenterZ=0 NormalX=0 NormalY=0 NormalZ=1 AngleXU=0 Radius=2.8
    g12: Circle CenterX=5 CenterY=7 CenterZ=0 NormalX=0 NormalY=0 NormalZ=1 AngleXU=0 Radius=2.8
    g13: LineSegment StartX=0 StartY=38 StartZ=0 EndX=13 EndY=54 EndZ=0
    g14: LineSegment StartX=13 StartY=54 StartZ=0 EndX=37 EndY=54 EndZ=0
    g15: LineSegment StartX=37 StartY=54 StartZ=0 EndX=50 EndY=38 EndZ=0
    g16: LineSegment StartX=50 StartY=0 StartZ=0 EndX=37 EndY=-16 EndZ=0
    g17: LineSegment StartX=37 StartY=-16 StartZ=0 EndX=13 EndY=-16 EndZ=0
    g18: LineSegment StartX=13 StartY=-16 StartZ=0 EndX=0 EndY=1.8e-15 EndZ=0
  constraints (49):
    c: Vertical(g0)
    c: Vertical(g1)
    c: Distance(g0,g1) = 50
    c: Distance(g1,g1) = 38
    c: Coincident(g2,g3)
    c: Coincident(g3,g4)
    c: Coincident(g4,g5)
    c: Coincident(g5,g2)
    c: Horizontal(g2)
    c: Horizontal(g4)
    c: Vertical(g3)
    c: Vertical(g5)
    c: Distance(g3,g5) = 40
    c: Distance(g2,g4) = 24
    c: Coincident(g6,g2)
    c: Coincident(g7,g4)
    c: Coincident(g8,g3)
    c: Coincident(g8,g0)
    c: Equal(g8,g7)
    c: Equal(g7,g6)
    c: Coincident(g9,g4)
    c: Coincident(g10,g3)
    c: Coincident(g11,g2)
    c: Coincident(g12,g2)
    c: Equal(g12,g9)
    c: Equal(g12,g11)
    c: Equal(g12,g10)
    c: Diameter(g12) = 5.6
    c: Equal(g0,g1)
    c: Coincident(g1,g-1)
    c: Coincident(g6,g1)
    c: PointOnObject(g0,g-1)
    c: Coincident(g7,g1)
    c: Coincident(g13,g1)
    c: Coincident(g14,g13)
    c: Horizontal(g14)
    c: Coincident(g15,g14)
    c: Coincident(g15,g0)
    c: Coincident(g16,g0)
    c: Coincident(g17,g16)
    c: Horizontal(g17)
    c: Coincident(g18,g17)
    c: Coincident(g18,g1)
    c: DistanceY(g17,g13) = 70
    c: Equal(g14,g17)
    c: Equal(g13,g15)
    c: Equal(g15,g16)
    c: Equal(g16,g18)
    c: DistanceX(g14,g14) = 24
FEATURE [PartDesign::Pad] Pad
  Direction = (0,0,1)
  Length = 12
  Length2 = 10
  Profile = -> Sketch
  ReferenceAxis = -> Sketch [N_Axis]
  Refine = true
  Suppressed = false
  Type = 0
FEATURE [Sketcher::SketchObject] Sketch001
  ArcFitTolerance = 1e-06
  AttachmentSupport = -> [Pad]
  FullyConstrained = true
  MakeInternals = false
  MapMode = 5
  Placement = pos=(0,0,12) rot=(0,0,1;0rad)
  sketch-geometry (2):
    g0: Circle CenterX=25 CenterY=47 CenterZ=0 NormalX=0 NormalY=0 NormalZ=1 AngleXU=0 Radius=3.3
    g1: Circle CenterX=25 CenterY=-9 CenterZ=0 NormalX=0 NormalY=0 NormalZ=1 AngleXU=0 Radius=3.3
  constraints (6):
    c: DistanceY(g1,g0) = 56
    c: DistanceX(g1) = 25
    c: DistanceX(g1,g0) = 0
    c: DistanceY(g1,g-1) = 9
    c: Equal(g1,g0)
    c: Diameter(g1) = 6.6
FEATURE [PartDesign::Pocket] Pocket
  BaseFeature = -> Pad
  Direction = (0,0,-1)
  Length = 5
  Length2 = 5
  Profile = -> Sketch001
  ReferenceAxis = -> Sketch001 [N_Axis]
  Refine = true
  Suppressed = false
  Type = 1
FEATURE [Sketcher::SketchObject] Sketch002
  ArcFitTolerance = 1e-06
  AttachmentSupport = -> [Pocket]
  FullyConstrained = true
  MakeInternals = false
  MapMode = 5
  Placement = pos=(0,0,0) rot=(1,0,0;3.14159rad)
  expr: Constraints[0] = Sketch001.Constraints[0]
  expr: Constraints[1] = Sketch001.Constraints[1]
  expr: Constraints[2] = Sketch001.Constraints[2]
  expr: Constraints[5] = Sketch001.Constraints[5]
  sketch-geometry (16):
    g0: Circle [constr] CenterX=25 CenterY=9 CenterZ=0 NormalX=0 NormalY=0 NormalZ=1 AngleXU=0 Radius=3.3
    g1: Circle [constr] CenterX=25 CenterY=-47 CenterZ=0 NormalX=0 NormalY=0 NormalZ=1 AngleXU=0 Radius=3.3
    g2: LineSegment StartX=27.9734 StartY=-52.15 StartZ=0 EndX=30.9467 EndY=-47 EndZ=0
    g3: LineSegment StartX=30.9467 StartY=-47 StartZ=0 EndX=27.9734 EndY=-41.85 EndZ=0
    g4: LineSegment StartX=27.9734 StartY=-41.85 StartZ=0 EndX=22.0266 EndY=-41.85 EndZ=0
    g5: LineSegment StartX=22.0266 StartY=-41.85 StartZ=0 EndX=19.0533 EndY=-47 EndZ=0
    g6: LineSegment StartX=19.0533 StartY=-47 StartZ=0 EndX=22.0266 EndY=-52.15 EndZ=0
    g7: LineSegment StartX=22.0266 StartY=-52.15 StartZ=0 EndX=27.9734 EndY=-52.15 EndZ=0
    g8: Circle [constr] CenterX=25 CenterY=-47 CenterZ=0 NormalX=0 NormalY=0 NormalZ=1 AngleXU=0 Radius=5.94671
    g9: LineSegment StartX=27.9734 StartY=3.85 StartZ=0 EndX=30.9467 EndY=9 EndZ=0
    g10: LineSegment StartX=30.9467 StartY=9 StartZ=0 EndX=27.9734 EndY=14.15 EndZ=0
    g11: LineSegment StartX=27.9734 StartY=14.15 StartZ=0 EndX=22.0266 EndY=14.15 EndZ=0
    g12: LineSegment StartX=22.0266 StartY=14.15 StartZ=0 EndX=19.0533 EndY=9 EndZ=0
    g13: LineSegment StartX=19.0533 StartY=9 StartZ=0 EndX=22.0266 EndY=3.85 EndZ=0
    g14: LineSegment StartX=22.0266 StartY=3.85 StartZ=0 EndX=27.9734 EndY=3.85 EndZ=0
    g15: Circle [constr] CenterX=25 CenterY=9 CenterZ=0 NormalX=0 NormalY=0 NormalZ=1 AngleXU=0 Radius=5.94671
  constraints (38):
    c: DistanceY(g1,g0) = 56
    c: DistanceX(g1) = 25
    c: DistanceX(g1,g0) = 0
    c: DistanceY(g1,g-1) = 47
    c: Equal(g1,g0)
    c: Diameter(g1) = 6.6
    c: Coincident(g2,g3)
    c: Coincident(g3,g4)
    c: Coincident(g4,g5)
    c: Coincident(g5,g6)
    c: Coincident(g6,g7)
    c: Coincident(g7,g2)
    c: Equal(g2, g3-g7) x5
    c: PointOnObject(g2,g8)
    c: PointOnObject(g3,g8)
    c: PointOnObject(g4,g8)
    c: PointOnObject(g5,g8)
    c: PointOnObject(g6,g8)
    c: PointOnObject(g7,g8)
    c: Coincident(g8,g1)
    c: Distance(g4,g2) = 10.3
    c: Horizontal(g4)
    c: Coincident(g9,g10)
    c: Coincident(g10,g11)
    c: Coincident(g11,g12)
    c: Coincident(g12,g13)
    c: Coincident(g13,g14)
    c: Coincident(g14,g9)
    c: Equal(g9, g10-g14) x5
    c: PointOnObject(g9,g15)
    c: PointOnObject(g10,g15)
    c: PointOnObject(g11,g15)
    c: PointOnObject(g12,g15)
    c: PointOnObject(g13,g15)
    c: PointOnObject(g14,g15)
    c: Coincident(g15,g0)
    c: Horizontal(g11)
    c: Equal(g14,g4)
FEATURE [PartDesign::Pocket] Pocket001
  BaseFeature = -> Pocket
  Direction = (0,0,1)
  Length = 6
  Length2 = 5
  Profile = -> Sketch002
  ReferenceAxis = -> Sketch002 [N_Axis]
  Refine = true
  Suppressed = false
  Type = 0
FEATURE [PartDesign::Fillet] Fillet
  Base = -> Pocket001 [Edge46,Edge44,Edge8,Edge45,Edge43,Edge5,Edge1,Edge2]
  BaseFeature = -> Pocket001
  Radius = 4
  Refine = true
  SupportTransform = false
  Suppressed = false
  UseAllEdges = false
FEATURE [Sketcher::SketchObject] Sketch003
  ArcFitTolerance = 1e-06
  AttachmentSupport = -> [Fillet]
  FullyConstrained = true
  MakeInternals = false
  MapMode = 5
  Placement = pos=(0,0,12) rot=(0,0,1;0rad)
  sketch-geometry (4):
    g0: LineSegment StartX=37 StartY=54 StartZ=0 EndX=37 EndY=-16 EndZ=0
    g1: LineSegment StartX=37 StartY=-16 StartZ=0 EndX=50 EndY=-16 EndZ=0
    g2: LineSegment StartX=50 StartY=-16 StartZ=0 EndX=50 EndY=54 EndZ=0
    g3: LineSegment StartX=50 StartY=54 StartZ=0 EndX=37 EndY=54 EndZ=0
  constraints (12):
    c: Coincident(g0,g1)
    c: Coincident(g1,g2)
    c: Coincident(g2,g3)
    c: Coincident(g3,g0)
    c: Vertical(g0)
    c: Vertical(g2)
    c: Horizontal(g1)
    c: Horizontal(g3)
    c: Distance(g0,g2) = 13
    c: DistanceX(g1) = 50
    c: DistanceY(g0) = -16
    c: DistanceY(g0,g0) = 70
FEATURE [PartDesign::Pocket] Pocket002
  BaseFeature = -> Fillet
  Direction = (0,0,-1)
  Length = 5
  Length2 = 5
  Profile = -> Sketch003
  ReferenceAxis = -> Sketch003 [N_Axis]
  Refine = true
  Suppressed = false
  Type = 0
FEATURE [PartDesign::Body] Body  label="DSG16H_to_SH25"
  AllowCompound = false
  Group = -> [Sketch,Pad,Sketch001,Pocket,Sketch002,Pocket001,Fillet,Sketch003,Pocket002]
  Origin = -> Origin
  Tip = -> Pocket002
---- part ../parts_library/SC25UU_to_SH25.FCStd = doc fcstd_0d684ae2b9f6 ----
FCSTD DOCUMENT  (FreeCAD 1.0R39109 (Git))
Label: SC25UU_to_SH25
License: All rights reserved
LicenseURL: https://en.wikipedia.org/wiki/All_rights_reserved
objects: Sketcher::SketchObject×3, PartDesign::Pocket×2, PartDesign::Pad×1, PartDesign::Fillet×1, PartDesign::Body×1
note: 19 computed .brp shape members not serialized (recipe doc carries the construction recipe); baked Part::Feature solids carry a one-line shape summary decoded from their .brp

FEATURE [Sketcher::SketchObject] Sketch
  ArcFitTolerance = 1e-06
  AttachmentSupport = -> [XY_Plane]
  FullyConstrained = true
  MakeInternals = false
  MapMode = 5
  sketch-geometry (19):
    g0: LineSegment StartX=76 StartY=0 StartZ=0 EndX=76 EndY=67 EndZ=0
    g1: LineSegment StartX=0 StartY=67 StartZ=0 EndX=0 EndY=0 EndZ=0
    g2: LineSegment [constr] StartX=11 StartY=58.5 StartZ=0 EndX=11 EndY=8.5 EndZ=0
    g3: LineSegment [constr] StartX=11 StartY=8.5 StartZ=0 EndX=65 EndY=8.5 EndZ=0
    g4: LineSegment [constr] StartX=65 StartY=8.5 StartZ=0 EndX=65 EndY=58.5 EndZ=0
    g5: LineSegment [constr] StartX=65 StartY=58.5 StartZ=0 EndX=11 EndY=58.5 EndZ=0
    g6: Circle CenterX=11 CenterY=58.5 CenterZ=0 NormalX=0 NormalY=0 NormalZ=1 AngleXU=0 Radius=4.3
    g7: Circle CenterX=65 CenterY=58.5 CenterZ=0 NormalX=0 NormalY=0 NormalZ=1 AngleXU=0 Radius=4.3
    g8: Circle CenterX=65 CenterY=8.5 CenterZ=0 NormalX=0 NormalY=0 NormalZ=1 AngleXU=0 Radius=4.3
    g9: Circle CenterX=11 CenterY=8.5 CenterZ=0 NormalX=0 NormalY=0 NormalZ=1 AngleXU=0 Radius=4.3
    g10: LineSegment [constr] StartX=0 StartY=0 StartZ=0 EndX=11 EndY=8.5 EndZ=0
    g11: LineSegment [constr] StartX=65 StartY=58.5 StartZ=0 EndX=76 EndY=67 EndZ=0
    g12: LineSegment [constr] StartX=11 StartY=58.5 StartZ=0 EndX=0 EndY=67 EndZ=0
    g13: LineSegment StartX=0 StartY=67 StartZ=0 EndX=26 EndY=68.5 EndZ=0
    g14: LineSegment StartX=26 StartY=68.5 StartZ=0 EndX=50 EndY=68.5 EndZ=0
    g15: LineSegment StartX=50 StartY=68.5 StartZ=0 EndX=76 EndY=67 EndZ=0
    g16: LineSegment StartX=0 StartY=0 StartZ=0 EndX=26 EndY=-1.5 EndZ=0
    g17: LineSegment StartX=26 StartY=-1.5 StartZ=0 EndX=50 EndY=-1.5 EndZ=0
    g18: LineSegment StartX=50 StartY=-1.5 StartZ=0 EndX=76 EndY=0 EndZ=0
  constraints (49):
    c: Vertical(g0)
    c: Vertical(g1)
    c: Distance(g0,g1) = 76
    c: Distance(g1,g1) = 67
    c: Coincident(g2,g3)
    c: Coincident(g3,g4)
    c: Coincident(g4,g5)
    c: Coincident(g5,g2)
    c: Vertical(g2)
    c: Vertical(g4)
    c: Horizontal(g3)
    c: Horizontal(g5)
    c: Distance(g2,g4) = 54
    c: Distance(g3,g5) = 50
    c: Coincident(g6,g2)
    c: Coincident(g7,g4)
    c: Coincident(g8,g3)
    c: Coincident(g9,g2)
    c: Equal(g7,g8)
    c: Equal(g7,g9)
    c: Equal(g7,g6)
    c: Diameter(g7) = 8.6
    c: Coincident(g10,g2)
    c: Coincident(g11,g4)
    c: Coincident(g11,g0)
    c: Coincident(g12,g2)
    c: Equal(g12,g10)
    c: Equal(g12,g11)
    c: Coincident(g13,g1)
    c: Coincident(g14,g13)
    c: Horizontal(g14)
    c: Coincident(g15,g14)
    c: Coincident(g15,g0)
    c: Coincident(g16,g1)
    c: Coincident(g17,g16)
    c: Horizontal(g17)
    c: Coincident(g18,g17)
    c: Coincident(g18,g0)
    c: DistanceX(g17,g17) = 24
    c: Equal(g17,g14)
    c: Equal(g13,g15)
    c: Equal(g15,g18)
    c: Equal(g18,g16)
    c: Coincident(g1,g10)
    c: Coincident(g1,g-1)
    c: Coincident(g12,g1)
    c: PointOnObject(g0,g-1)
    c: Equal(g0,g1)
    c: DistanceY(g16,g13) = 70
FEATURE [PartDesign::Pad] Pad
  Direction = (0,0,1)
  Length = 10
  Length2 = 10
  Profile = -> Sketch
  ReferenceAxis = -> Sketch [N_Axis]
  Refine = true
  Suppressed = false
  Type = 0
FEATURE [Sketcher::SketchObject] Sketch001
  ArcFitTolerance = 1e-06
  AttachmentSupport = -> [Pad]
  FullyConstrained = true
  MakeInternals = false
  MapMode = 5
  Placement = pos=(0,0,10) rot=(0,0,1;0rad)
  sketch-geometry (2):
    g0: Circle CenterX=38 CenterY=61.5 CenterZ=0 NormalX=0 NormalY=0 NormalZ=1 AngleXU=0 Radius=3.3
    g1: Circle CenterX=38 CenterY=5.5 CenterZ=0 NormalX=0 NormalY=0 NormalZ=1 AngleXU=0 Radius=3.3
  constraints (6):
    c: DistanceY(g1,g0) = 56
    c: Equal(g1,g0)
    c: Diameter(g1) = 6.6
    c: DistanceY(g1) = 5.5
    c: DistanceX(g1) = 38
    c: DistanceX(g0,g1) = 0
FEATURE [PartDesign::Pocket] Pocket
  BaseFeature = -> Pad
  Direction = (0,0,-1)
  Length = 5
  Length2 = 5
  Profile = -> Sketch001
  ReferenceAxis = -> Sketch001 [N_Axis]
  Refine = true
  Suppressed = false
  Type = 1
FEATURE [Sketcher::SketchObject] Sketch002
  ArcFitTolerance = 1e-06
  AttachmentSupport = -> [Pocket]
  FullyConstrained = true
  MakeInternals = false
  MapMode = 5
  Placement = pos=(0,0,0) rot=(1,0,0;3.14159rad)
  expr: Constraints[2] = Sketch001.Constraints[2]
  expr: Constraints[4] = Sketch001.Constraints[4]
  expr: Constraints[5] = Sketch001.Constraints[5]
  sketch-geometry (16):
    g0: Circle [constr] CenterX=38 CenterY=-61.5 CenterZ=0 NormalX=0 NormalY=0 NormalZ=1 AngleXU=0 Radius=3.3
    g1: Circle [constr] CenterX=38 CenterY=-5.5 CenterZ=0 NormalX=0 NormalY=0 NormalZ=1 AngleXU=0 Radius=3.3
    g2: LineSegment StartX=40.9734 StartY=-10.65 StartZ=0 EndX=43.9467 EndY=-5.5 EndZ=0
    g3: LineSegment StartX=43.9467 StartY=-5.5 StartZ=0 EndX=40.9734 EndY=-0.35 EndZ=0
    g4: LineSegment StartX=40.9734 StartY=-0.35 StartZ=0 EndX=35.0266 EndY=-0.35 EndZ=0
    g5: LineSegment StartX=35.0266 StartY=-0.35 StartZ=0 EndX=32.0533 EndY=-5.5 EndZ=0
    g6: LineSegment StartX=32.0533 StartY=-5.5 StartZ=0 EndX=35.0266 EndY=-10.65 EndZ=0
    g7: LineSegment StartX=35.0266 StartY=-10.65 StartZ=0 EndX=40.9734 EndY=-10.65 EndZ=0
    g8: Circle [constr] CenterX=38 CenterY=-5.5 CenterZ=0 NormalX=0 NormalY=0 NormalZ=1 AngleXU=0 Radius=5.94671
    g9: LineSegment StartX=43.9467 StartY=-61.5 StartZ=0 EndX=40.9734 EndY=-56.35 EndZ=0
    g10: LineSegment StartX=40.9734 StartY=-56.35 StartZ=0 EndX=35.0266 EndY=-56.35 EndZ=0
    g11: LineSegment StartX=35.0266 StartY=-56.35 StartZ=0 EndX=32.0533 EndY=-61.5 EndZ=0
    g12: LineSegment StartX=32.0533 StartY=-61.5 StartZ=0 EndX=35.0266 EndY=-66.65 EndZ=0
    g13: LineSegment StartX=35.0266 StartY=-66.65 StartZ=0 EndX=40.9734 EndY=-66.65 EndZ=0
    g14: LineSegment StartX=40.9734 StartY=-66.65 StartZ=0 EndX=43.9467 EndY=-61.5 EndZ=0
    g15: Circle [constr] CenterX=38 CenterY=-61.5 CenterZ=0 NormalX=0 NormalY=0 NormalZ=1 AngleXU=0 Radius=5.94671
  constraints (38):
    c: DistanceY(g1,g0) = -56
    c: Equal(g1,g0)
    c: Diameter(g1) = 6.6
    c: DistanceY(g1) = -5.5
    c: DistanceX(g1) = 38
    c: DistanceX(g0,g1) = 0
    c: Coincident(g2,g3)
    c: Coincident(g3,g4)
    c: Coincident(g4,g5)
    c: Coincident(g5,g6)
    c: Coincident(g6,g7)
    c: Coincident(g7,g2)
    c: Equal(g2, g3-g7) x5
    c: PointOnObject(g2,g8)
    c: PointOnObject(g3,g8)
    c: PointOnObject(g4,g8)
    c: PointOnObject(g5,g8)
    c: PointOnObject(g6,g8)
    c: PointOnObject(g7,g8)
    c: Coincident(g8,g1)
    c: Coincident(g9,g10)
    c: Coincident(g10,g11)
    c: Coincident(g11,g12)
    c: Coincident(g12,g13)
    c: Coincident(g13,g14)
    c: Coincident(g14,g9)
    c: Equal(g9, g10-g14) x5
    c: PointOnObject(g9,g15)
    c: PointOnObject(g10,g15)
    c: PointOnObject(g11,g15)
    c: PointOnObject(g12,g15)
    c: PointOnObject(g13,g15)
    c: PointOnObject(g14,g15)
    c: Coincident(g15,g0)
    c: Distance(g10,g9) = 10.3
    c: Horizontal(g10)
    c: Equal(g10,g4)
    c: Horizontal(g4)
FEATURE [PartDesign::Pocket] Pocket001
  BaseFeature = -> Pocket
  Direction = (0,0,1)
  Length = 5.2
  Length2 = 5
  Profile = -> Sketch002
  ReferenceAxis = -> Sketch002 [N_Axis]
  Refine = true
  Suppressed = false
  Type = 0
FEATURE [PartDesign::Fillet] Fillet
  Base = -> Pocket001 [Edge1,Edge2,Edge46,Edge45]
  BaseFeature = -> Pocket001
  Radius = 3
  Refine = true
  SupportTransform = false
  Suppressed = false
  UseAllEdges = false
FEATURE [PartDesign::Body] Body  label="SC25UU_to_SH25"
  AllowCompound = false
  Group = -> [Sketch,Pad,Sketch001,Pocket,Sketch002,Pocket001,Fillet]
  Origin = -> Origin
  Tip = -> Fillet
---- part ../parts_library/coupler.FCStd = doc fcstd_cd94560a88da ----
FCSTD DOCUMENT  (FreeCAD 1.0R39109 (Git))
Label: coupler
License: All rights reserved
LicenseURL: https://en.wikipedia.org/wiki/All_rights_reserved
objects: Sketcher::SketchObject×3, PartDesign::Pocket×2, PartDesign::Pad×1, PartDesign::Body×1
note: 16 computed .brp shape members not serialized (recipe doc carries the construction recipe); baked Part::Feature solids carry a one-line shape summary decoded from their .brp

FEATURE [Sketcher::SketchObject] Sketch
  ArcFitTolerance = 1e-06
  AttachmentSupport = -> [XZ_Plane]
  FullyConstrained = true
  MakeInternals = false
  MapMode = 5
  Placement = pos=(0,0,0) rot=(1,0,0;1.5708rad)
  sketch-geometry (1):
    g0: Circle CenterX=0 CenterY=0 CenterZ=0 NormalX=0 NormalY=0 NormalZ=1 AngleXU=0 Radius=17.5
  constraints (2):
    c: Coincident(g0,g-1)
    c: Diameter(g0) = 35
FEATURE [PartDesign::Pad] Pad
  Direction = (0,-1,2e-16)
  Length = 50
  Length2 = 10
  Placement = pos=(0,0,0) rot=(1,0,0;1.5708rad)
  Profile = -> Sketch
  ReferenceAxis = -> Sketch [N_Axis]
  Refine = true
  Suppressed = false
  Type = 0
FEATURE [Sketcher::SketchObject] Sketch001
  ArcFitTolerance = 1e-06
  AttachmentSupport = -> [Pad]
  FullyConstrained = true
  MakeInternals = false
  MapMode = 5
  Placement = pos=(0,-50,0) rot=(1,0,0;1.5708rad)
  sketch-geometry (1):
    g0: Circle CenterX=0 CenterY=0 CenterZ=0 NormalX=0 NormalY=0 NormalZ=1 AngleXU=0 Radius=9.5
  constraints (2):
    c: Coincident(g0,g-1)
    c: Diameter(g0) = 19
FEATURE [PartDesign::Pocket] Pocket
  BaseFeature = -> Pad
  Direction = (0,1,-2e-16)
  Length = 18.5
  Length2 = 5
  Placement = pos=(0,0,0) rot=(1,0,0;1.5708rad)
  Profile = -> Sketch001
  ReferenceAxis = -> Sketch001 [N_Axis]
  Refine = true
  Suppressed = false
  Type = 0
FEATURE [Sketcher::SketchObject] Sketch002
  ArcFitTolerance = 1e-06
  AttachmentSupport = -> [Pocket]
  FullyConstrained = true
  MakeInternals = false
  MapMode = 5
  Placement = pos=(0,0,0) rot=(-1,0,0;1.5708rad)
  sketch-geometry (1):
    g0: Circle CenterX=0 CenterY=0 CenterZ=0 NormalX=0 NormalY=0 NormalZ=1 AngleXU=0 Radius=5
  constraints (2):
    c: Diameter(g0) = 10
    c: Coincident(g0,g-1)
FEATURE [PartDesign::Pocket] Pocket001
  BaseFeature = -> Pocket
  Direction = (0,-1,-2e-16)
  Length = 18.5
  Length2 = 5
  Placement = pos=(0,0,0) rot=(1,0,0;1.5708rad)
  Profile = -> Sketch002
  ReferenceAxis = -> Sketch002 [N_Axis]
  Refine = true
  Suppressed = false
  Type = 0
FEATURE [PartDesign::Body] Body  label="coupler_10x19"
  AllowCompound = false
  Group = -> [Sketch,Pad,Sketch001,Pocket,Sketch002,Pocket001]
  Origin = -> Origin
  Tip = -> Pocket001
---- part ../parts_library/linear_shaft.FCStd = doc fcstd_3204002d9ceb ----
FCSTD DOCUMENT  (FreeCAD 1.0R39109 (Git))
Label: linear_shaft
License: All rights reserved
LicenseURL: https://en.wikipedia.org/wiki/All_rights_reserved
objects: Sketcher::SketchObject×2, PartDesign::Pad×2, PartDesign::Body×2
note: 12 computed .brp shape members not serialized (recipe doc carries the construction recipe); baked Part::Feature solids carry a one-line shape summary decoded from their .brp

FEATURE [Sketcher::SketchObject] Sketch
  ArcFitTolerance = 1e-06
  AttachmentSupport = -> [XZ_Plane]
  FullyConstrained = true
  MakeInternals = false
  MapMode = 5
  Placement = pos=(0,0,0) rot=(1,0,0;1.5708rad)
  sketch-geometry (1):
    g0: Circle CenterX=0 CenterY=0 CenterZ=0 NormalX=0 NormalY=0 NormalZ=1 AngleXU=0 Radius=12.5
  constraints (2):
    c: Diameter(g0) = 25
    c: Coincident(g0,g-1)
FEATURE [PartDesign::Pad] Pad
  Direction = (0,-1,2e-16)
  Length = 500
  Length2 = 10
  Placement = pos=(0,0,0) rot=(1,0,0;1.5708rad)
  Profile = -> Sketch
  ReferenceAxis = -> Sketch [N_Axis]
  Refine = true
  Suppressed = false
  Type = 0
FEATURE [PartDesign::Body] Body  label="linear_shaft_25x500"
  AllowCompound = false
  Group = -> [Sketch,Pad]
  Origin = -> Origin
  Tip = -> Pad
FEATURE [Sketcher::SketchObject] Sketch001
  ArcFitTolerance = 1e-06
  AttachmentSupport = -> [XZ_Plane001]
  FullyConstrained = true
  MakeInternals = false
  MapMode = 5
  Placement = pos=(0,0,0) rot=(1,0,0;1.5708rad)
  sketch-geometry (1):
    g0: Circle CenterX=0 CenterY=0 CenterZ=0 NormalX=0 NormalY=0 NormalZ=1 AngleXU=0 Radius=12.5
  constraints (2):
    c: Diameter(g0) = 25
    c: Coincident(g0,g-1)
FEATURE [PartDesign::Pad] Pad001
  Direction = (0,-1,2e-16)
  Length = 428
  Length2 = 10
  Placement = pos=(0,0,0) rot=(1,0,0;1.5708rad)
  Profile = -> Sketch001
  ReferenceAxis = -> Sketch001 [N_Axis]
  Refine = true
  Suppressed = false
  Type = 0
FEATURE [PartDesign::Body] Body001  label="linear_shaft_25x428"
  AllowCompound = false
  Group = -> [Sketch001,Pad001]
  Origin = -> Origin001
  Tip = -> Pad001
---- part sway_SC25UU_to_SH25_with_plate.FCStd = doc fcstd_8c454a364cee ----
FCSTD DOCUMENT  (FreeCAD 1.0R39109 (Git))
Label: sway_SC25UU_to_SH25_with_plate
License: All rights reserved
LicenseURL: https://en.wikipedia.org/wiki/All_rights_reserved
objects: Sketcher::SketchObject×4, PartDesign::Pocket×3, PartDesign::Pad×1, PartDesign::Fillet×1, PartDesign::Body×1
note: 24 computed .brp shape members not serialized (recipe doc carries the construction recipe); baked Part::Feature solids carry a one-line shape summary decoded from their .brp

FEATURE [Sketcher::SketchObject] Sketch
  ArcFitTolerance = 1e-06
  AttachmentSupport = -> [XY_Plane]
  FullyConstrained = true
  MakeInternals = false
  MapMode = 5
  sketch-geometry (19):
    g0: LineSegment StartX=76 StartY=0 StartZ=0 EndX=76 EndY=67 EndZ=0
    g1: LineSegment StartX=0 StartY=67 StartZ=0 EndX=0 EndY=0 EndZ=0
    g2: LineSegment [constr] StartX=11 StartY=58.5 StartZ=0 EndX=11 EndY=8.5 EndZ=0
    g3: LineSegment [constr] StartX=11 StartY=8.5 StartZ=0 EndX=65 EndY=8.5 EndZ=0
    g4: LineSegment [constr] StartX=65 StartY=8.5 StartZ=0 EndX=65 EndY=58.5 EndZ=0
    g5: LineSegment [constr] StartX=65 StartY=58.5 StartZ=0 EndX=11 EndY=58.5 EndZ=0
    g6: Circle CenterX=11 CenterY=58.5 CenterZ=0 NormalX=0 NormalY=0 NormalZ=1 AngleXU=0 Radius=4.3
    g7: Circle CenterX=65 CenterY=58.5 CenterZ=0 NormalX=0 NormalY=0 NormalZ=1 AngleXU=0 Radius=4.3
    g8: Circle CenterX=65 CenterY=8.5 CenterZ=0 NormalX=0 NormalY=0 NormalZ=1 AngleXU=0 Radius=4.3
    g9: Circle CenterX=11 CenterY=8.5 CenterZ=0 NormalX=0 NormalY=0 NormalZ=1 AngleXU=0 Radius=4.3
    g10: LineSegment [constr] StartX=0 StartY=0 StartZ=0 EndX=11 EndY=8.5 EndZ=0
    g11: LineSegment [constr] StartX=65 StartY=58.5 StartZ=0 EndX=76 EndY=67 EndZ=0
    g12: LineSegment [constr] StartX=11 StartY=58.5 StartZ=0 EndX=0 EndY=67 EndZ=0
    g13: LineSegment StartX=0 StartY=67 StartZ=0 EndX=26 EndY=68.5 EndZ=0
    g14: LineSegment StartX=26 StartY=68.5 StartZ=0 EndX=50 EndY=68.5 EndZ=0
    g15: LineSegment StartX=50 StartY=68.5 StartZ=0 EndX=76 EndY=67 EndZ=0
    g16: LineSegment StartX=0 StartY=0 StartZ=0 EndX=26 EndY=-1.5 EndZ=0
    g17: LineSegment StartX=26 StartY=-1.5 StartZ=0 EndX=50 EndY=-1.5 EndZ=0
    g18: LineSegment StartX=50 StartY=-1.5 StartZ=0 EndX=76 EndY=0 EndZ=0
  constraints (49):
    c: Vertical(g0)
    c: Vertical(g1)
    c: Distance(g0,g1) = 76
    c: Distance(g1,g1) = 67
    c: Coincident(g2,g3)
    c: Coincident(g3,g4)
    c: Coincident(g4,g5)
    c: Coincident(g5,g2)
    c: Vertical(g2)
    c: Vertical(g4)
    c: Horizontal(g3)
    c: Horizontal(g5)
    c: Distance(g2,g4) = 54
    c: Distance(g3,g5) = 50
    c: Coincident(g6,g2)
    c: Coincident(g7,g4)
    c: Coincident(g8,g3)
    c: Coincident(g9,g2)
    c: Equal(g7,g8)
    c: Equal(g7,g9)
    c: Equal(g7,g6)
    c: Diameter(g7) = 8.6
    c: Coincident(g10,g2)
    c: Coincident(g11,g4)
    c: Coincident(g11,g0)
    c: Coincident(g12,g2)
    c: Equal(g12,g10)
    c: Equal(g12,g11)
    c: Coincident(g13,g1)
    c: Coincident(g14,g13)
    c: Horizontal(g14)
    c: Coincident(g15,g14)
    c: Coincident(g15,g0)
    c: Coincident(g16,g1)
    c: Coincident(g17,g16)
    c: Horizontal(g17)
    c: Coincident(g18,g17)
    c: Coincident(g18,g0)
    c: DistanceX(g17,g17) = 24
    c: Equal(g17,g14)
    c: Equal(g13,g15)
    c: Equal(g15,g18)
    c: Equal(g18,g16)
    c: Coincident(g1,g10)
    c: Coincident(g1,g-1)
    c: Coincident(g12,g1)
    c: PointOnObject(g0,g-1)
    c: Equal(g0,g1)
    c: DistanceY(g16,g13) = 70
FEATURE [PartDesign::Pad] Pad
  Direction = (0,0,1)
  Length = 10
  Length2 = 10
  Profile = -> Sketch
  ReferenceAxis = -> Sketch [N_Axis]
  Refine = true
  Suppressed = false
  Type = 0
FEATURE [Sketcher::SketchObject] Sketch001
  ArcFitTolerance = 1e-06
  AttachmentSupport = -> [Pad]
  FullyConstrained = true
  MakeInternals = false
  MapMode = 5
  Placement = pos=(0,0,10) rot=(0,0,1;0rad)
  sketch-geometry (2):
    g0: Circle CenterX=38 CenterY=61.5 CenterZ=0 NormalX=0 NormalY=0 NormalZ=1 AngleXU=0 Radius=3.3
    g1: Circle CenterX=38 CenterY=5.5 CenterZ=0 NormalX=0 NormalY=0 NormalZ=1 AngleXU=0 Radius=3.3
  constraints (6):
    c: DistanceY(g1,g0) = 56
    c: Equal(g1,g0)
    c: Diameter(g1) = 6.6
    c: DistanceY(g1) = 5.5
    c: DistanceX(g1) = 38
    c: DistanceX(g0,g1) = 0
FEATURE [PartDesign::Pocket] Pocket
  BaseFeature = -> Pad
  Direction = (0,0,-1)
  Length = 5
  Length2 = 5
  Profile = -> Sketch001
  ReferenceAxis = -> Sketch001 [N_Axis]
  Refine = true
  Suppressed = false
  Type = 1
FEATURE [Sketcher::SketchObject] Sketch002
  ArcFitTolerance = 1e-06
  AttachmentSupport = -> [Pocket]
  FullyConstrained = true
  MakeInternals = false
  MapMode = 5
  Placement = pos=(0,0,0) rot=(1,0,0;3.14159rad)
  expr: Constraints[2] = Sketch001.Constraints[2]
  expr: Constraints[4] = Sketch001.Constraints[4]
  expr: Constraints[5] = Sketch001.Constraints[5]
  sketch-geometry (16):
    g0: Circle [constr] CenterX=38 CenterY=-61.5 CenterZ=0 NormalX=0 NormalY=0 NormalZ=1 AngleXU=0 Radius=3.3
    g1: Circle [constr] CenterX=38 CenterY=-5.5 CenterZ=0 NormalX=0 NormalY=0 NormalZ=1 AngleXU=0 Radius=3.3
    g2: LineSegment StartX=40.9734 StartY=-10.65 StartZ=0 EndX=43.9467 EndY=-5.5 EndZ=0
    g3: LineSegment StartX=43.9467 StartY=-5.5 StartZ=0 EndX=40.9734 EndY=-0.35 EndZ=0
    g4: LineSegment StartX=40.9734 StartY=-0.35 StartZ=0 EndX=35.0266 EndY=-0.35 EndZ=0
    g5: LineSegment StartX=35.0266 StartY=-0.35 StartZ=0 EndX=32.0533 EndY=-5.5 EndZ=0
    g6: LineSegment StartX=32.0533 StartY=-5.5 StartZ=0 EndX=35.0266 EndY=-10.65 EndZ=0
    g7: LineSegment StartX=35.0266 StartY=-10.65 StartZ=0 EndX=40.9734 EndY=-10.65 EndZ=0
    g8: Circle [constr] CenterX=38 CenterY=-5.5 CenterZ=0 NormalX=0 NormalY=0 NormalZ=1 AngleXU=0 Radius=5.94671
    g9: LineSegment StartX=43.9467 StartY=-61.5 StartZ=0 EndX=40.9734 EndY=-56.35 EndZ=0
    g10: LineSegment StartX=40.9734 StartY=-56.35 StartZ=0 EndX=35.0266 EndY=-56.35 EndZ=0
    g11: LineSegment StartX=35.0266 StartY=-56.35 StartZ=0 EndX=32.0533 EndY=-61.5 EndZ=0
    g12: LineSegment StartX=32.0533 StartY=-61.5 StartZ=0 EndX=35.0266 EndY=-66.65 EndZ=0
    g13: LineSegment StartX=35.0266 StartY=-66.65 StartZ=0 EndX=40.9734 EndY=-66.65 EndZ=0
    g14: LineSegment StartX=40.9734 StartY=-66.65 StartZ=0 EndX=43.9467 EndY=-61.5 EndZ=0
    g15: Circle [constr] CenterX=38 CenterY=-61.5 CenterZ=0 NormalX=0 NormalY=0 NormalZ=1 AngleXU=0 Radius=5.94671
  constraints (38):
    c: DistanceY(g1,g0) = -56
    c: Equal(g1,g0)
    c: Diameter(g1) = 6.6
    c: DistanceY(g1) = -5.5
    c: DistanceX(g1) = 38
    c: DistanceX(g0,g1) = 0
    c: Coincident(g2,g3)
    c: Coincident(g3,g4)
    c: Coincident(g4,g5)
    c: Coincident(g5,g6)
    c: Coincident(g6,g7)
    c: Coincident(g7,g2)
    c: Equal(g2, g3-g7) x5
    c: PointOnObject(g2,g8)
    c: PointOnObject(g3,g8)
    c: PointOnObject(g4,g8)
    c: PointOnObject(g5,g8)
    c: PointOnObject(g6,g8)
    c: PointOnObject(g7,g8)
    c: Coincident(g8,g1)
    c: Coincident(g9,g10)
    c: Coincident(g10,g11)
    c: Coincident(g11,g12)
    c: Coincident(g12,g13)
    c: Coincident(g13,g14)
    c: Coincident(g14,g9)
    c: Equal(g9, g10-g14) x5
    c: PointOnObject(g9,g15)
    c: PointOnObject(g10,g15)
    c: PointOnObject(g11,g15)
    c: PointOnObject(g12,g15)
    c: PointOnObject(g13,g15)
    c: PointOnObject(g14,g15)
    c: Coincident(g15,g0)
    c: Distance(g10,g9) = 10.3
    c: Horizontal(g10)
    c: Equal(g10,g4)
    c: Horizontal(g4)
FEATURE [PartDesign::Pocket] Pocket001
  BaseFeature = -> Pocket
  Direction = (0,0,1)
  Length = 5.2
  Length2 = 5
  Profile = -> Sketch002
  ReferenceAxis = -> Sketch002 [N_Axis]
  Refine = true
  Suppressed = false
  Type = 0
FEATURE [PartDesign::Fillet] Fillet
  Base = -> Pocket001 [Edge1,Edge2,Edge46,Edge45]
  BaseFeature = -> Pocket001
  Radius = 3
  Refine = true
  SupportTransform = false
  Suppressed = false
  UseAllEdges = false
FEATURE [Sketcher::SketchObject] Sketch003
  ArcFitTolerance = 1e-06
  AttachmentSupport = -> [Fillet]
  FullyConstrained = true
  MakeInternals = false
  MapMode = 5
  Placement = pos=(0,0,10) rot=(0,0,1;0rad)
  sketch-geometry (4):
    g0: LineSegment StartX=0 StartY=-1.5 StartZ=0 EndX=26 EndY=-1.5 EndZ=0
    g1: LineSegment StartX=26 StartY=-1.5 StartZ=0 EndX=26 EndY=68.5 EndZ=0
    g2: LineSegment StartX=26 StartY=68.5 StartZ=0 EndX=0 EndY=68.5 EndZ=0
    g3: LineSegment StartX=0 StartY=68.5 StartZ=0 EndX=0 EndY=-1.5 EndZ=0
  constraints (12):
    c: Coincident(g0,g1)
    c: Coincident(g1,g2)
    c: Coincident(g2,g3)
    c: Coincident(g3,g0)
    c: Horizontal(g0)
    c: Horizontal(g2)
    c: Vertical(g1)
    c: Vertical(g3)
    c: Distance(g1,g3) = 26
    c: PointOnObject(g0,g-2)
    c: DistanceY(g0,g-1) = 1.5
    c: DistanceY(g3,g3) = 70
FEATURE [PartDesign::Pocket] Pocket002
  BaseFeature = -> Fillet
  Direction = (0,0,-1)
  Length = 5
  Length2 = 5
  Profile = -> Sketch003
  ReferenceAxis = -> Sketch003 [N_Axis]
  Refine = true
  Suppressed = false
  Type = 0
FEATURE [PartDesign::Body] Body  label="sway_SC25UU_to_SH25_with_plate"
  AllowCompound = false
  Group = -> [Sketch,Pad,Sketch001,Pocket,Sketch002,Pocket001,Fillet,Sketch003,Pocket002]
  Origin = -> Origin
  Tip = -> Pocket002
---- part sway_motor_mount_bottom.FCStd = doc fcstd_771a3c9189b0 ----
FCSTD DOCUMENT  (FreeCAD 1.0R39109 (Git))
Label: sway_motor_mount_bottom
License: All rights reserved
LicenseURL: https://en.wikipedia.org/wiki/All_rights_reserved
objects: Sketcher::SketchObject×3, PartDesign::Pocket×2, PartDesign::Fillet×2, PartDesign::Pad×1, PartDesign::Body×1
note: 22 computed .brp shape members not serialized (recipe doc carries the construction recipe); baked Part::Feature solids carry a one-line shape summary decoded from their .brp

FEATURE [Sketcher::SketchObject] Sketch
  ArcFitTolerance = 1e-06
  AttachmentSupport = -> [XZ_Plane]
  FullyConstrained = true
  MakeInternals = false
  MapMode = 5
  Placement = pos=(0,0,0) rot=(1,0,0;1.5708rad)
  sketch-geometry (30):
    g0: LineSegment [constr] StartX=-66.2 StartY=5 StartZ=0 EndX=-66.2 EndY=-5 EndZ=0
    g1: LineSegment [constr] StartX=-66.2 StartY=-5 StartZ=0 EndX=-40 EndY=-5 EndZ=0
    g2: LineSegment [constr] StartX=-40 StartY=-5 StartZ=0 EndX=-40 EndY=5 EndZ=0
    g3: LineSegment [constr] StartX=-40 StartY=5 StartZ=0 EndX=-66.2 EndY=5 EndZ=0
    g4: LineSegment [constr] StartX=40 StartY=5 StartZ=0 EndX=40 EndY=-5 EndZ=0
    g5: LineSegment [constr] StartX=40 StartY=-5 StartZ=0 EndX=66.2 EndY=-5 EndZ=0
    g6: LineSegment [constr] StartX=66.2 StartY=-5 StartZ=0 EndX=66.2 EndY=5 EndZ=0
    g7: LineSegment [constr] StartX=66.2 StartY=5 StartZ=0 EndX=40 EndY=5 EndZ=0
    g8: LineSegment [constr] StartX=-40 StartY=-5 StartZ=0 EndX=0 EndY=0 EndZ=0
    g9: LineSegment [constr] StartX=0 StartY=0 StartZ=0 EndX=40 EndY=-5 EndZ=0
    g10: LineSegment [constr] StartX=-40 StartY=60 StartZ=0 EndX=-40 EndY=-20 EndZ=0
    g11: LineSegment [constr] StartX=-40 StartY=-20 StartZ=0 EndX=40 EndY=-20 EndZ=0
    g12: LineSegment [constr] StartX=40 StartY=-20 StartZ=0 EndX=40 EndY=60 EndZ=0
    g13: LineSegment [constr] StartX=40 StartY=60 StartZ=0 EndX=-40 EndY=60 EndZ=0
    g14: LineSegment StartX=40.4 StartY=-5.4 StartZ=0 EndX=65.4 EndY=-5.4 EndZ=0
    g15: LineSegment StartX=65.4 StartY=-5.4 StartZ=0 EndX=65.4 EndY=-15.4 EndZ=0
    g16: LineSegment StartX=-65.4 StartY=-15.4 StartZ=0 EndX=-65.4 EndY=-5.4 EndZ=0
    g17: LineSegment StartX=-65.4 StartY=-5.4 StartZ=0 EndX=-40.4 EndY=-5.4 EndZ=0
    g18: ArcOfCircle [constr] CenterX=-40 CenterY=-20 CenterZ=0 NormalX=0 NormalY=0 NormalZ=1 AngleXU=0 Radius=14 StartAngle=0 EndAngle=1.5708
    g19: ArcOfCircle [constr] CenterX=-40 CenterY=60 CenterZ=0 NormalX=0 NormalY=0 NormalZ=1 AngleXU=0 Radius=14 StartAngle=4.71239 EndAngle=6.28319
    g20: ArcOfCircle [constr] CenterX=40 CenterY=-20 CenterZ=0 NormalX=0 NormalY=0 NormalZ=1 AngleXU=0 Radius=14 StartAngle=1.5708 EndAngle=3.14159
    g21: ArcOfCircle [constr] CenterX=40 CenterY=60 CenterZ=0 NormalX=0 NormalY=0 NormalZ=1 AngleXU=0 Radius=14 StartAngle=3.14159 EndAngle=4.71239
    g22: ArcOfCircle CenterX=-40.4 CenterY=-20.4 CenterZ=0 NormalX=0 NormalY=0 NormalZ=1 AngleXU=0 Radius=14 StartAngle=0 EndAngle=1.5708
    g23: ArcOfCircle CenterX=40.4 CenterY=-20.4 CenterZ=0 NormalX=0 NormalY=0 NormalZ=1 AngleXU=0 Radius=14 StartAngle=1.5708 EndAngle=3.14159
    g24: LineSegment StartX=-40.4 StartY=-6.4 StartZ=0 EndX=-40.4 EndY=-5.4 EndZ=0
    g25: LineSegment StartX=-26.4 StartY=-20.4 StartZ=0 EndX=26.4 EndY=-20.4 EndZ=0
    g26: LineSegment StartX=40.4 StartY=-6.4 StartZ=0 EndX=40.4 EndY=-5.4 EndZ=0
    g27: LineSegment StartX=-65.4 StartY=-15.4 StartZ=0 EndX=-26.4 EndY=-25.4 EndZ=0
    g28: LineSegment StartX=-26.4 StartY=-25.4 StartZ=0 EndX=26.4 EndY=-25.4 EndZ=0
    g29: LineSegment StartX=26.4 StartY=-25.4 StartZ=0 EndX=65.4 EndY=-15.4 EndZ=0
  constraints (94):
    c: Coincident(g0,g1)
    c: Coincident(g1,g2)
    c: Coincident(g2,g3)
    c: Coincident(g3,g0)
    c: Vertical(g0)
    c: Vertical(g2)
    c: Horizontal(g1)
    c: Horizontal(g3)
    c: Coincident(g4,g5)
    c: Coincident(g5,g6)
    c: Coincident(g6,g7)
    c: Coincident(g7,g4)
    c: Vertical(g4)
    c: Vertical(g6)
    c: Horizontal(g5)
    c: Horizontal(g7)
    c: Equal(g2,g4)
    c: DistanceY(g0,g0) = 10
    c: DistanceX(g2,g4) = 80
    c: DistanceY(g2,g4) = 0
    c: Coincident(g8,g1)
    c: Coincident(g8,g-1)
    c: Coincident(g9,g8)
    c: Coincident(g9,g4)
    c: Equal(g9,g8)
    c: Coincident(g10,g11)
    c: Coincident(g11,g12)
    c: Coincident(g12,g13)
    c: Coincident(g13,g10)
    c: Vertical(g10)
    c: Vertical(g12)
    c: Horizontal(g11)
    c: Horizontal(g13)
    c: PointOnObject(g2,g10)
    c: PointOnObject(g4,g12)
    c: Equal(g13,g10)
    c: DistanceY(g2) = 5
    c: Horizontal(g14)
    c: Coincident(g14,g15)
    c: Vertical(g15)
    c: Vertical(g16)
    c: Coincident(g16,g17)
    c: Horizontal(g17)
    c: DistanceY(g17,g1) = 0.4
    c: Equal(g16,g15)
    c: DistanceY(g16,g16) = 10
    c: Coincident(g18,g10)
    c: PointOnObject(g18,g10)
    c: PointOnObject(g18,g11)
    c: Diameter(g18) = 28
    c: Coincident(g19,g10)
    c: PointOnObject(g19,g13)
    c: PointOnObject(g19,g10)
    c: Coincident(g20,g11)
    c: PointOnObject(g20,g11)
    c: PointOnObject(g20,g12)
    c: Coincident(g21,g12)
    c: PointOnObject(g21,g13)
    c: PointOnObject(g21,g12)
    c: Equal(g18,g20)
    c: Equal(g20,g21)
    c: Equal(g21,g19)
    c: DistanceX(g17,g1) = 0.4
    c: Coincident(g24,g22)
    c: Coincident(g24,g17)
    c: Vertical(g24)
    c: DistanceY(g22,g18) = 0.4
    c: Coincident(g25,g22)
    c: Coincident(g25,g23)
    c: Horizontal(g25)
    c: DistanceY(g22,g18) = 0.4
    c: Perpendicular(g22,g24)
    c: Perpendicular(g22,g25)
    c: Perpendicular(g23,g25)
    c: Coincident(g26,g23)
    c: Coincident(g26,g14)
    c: Vertical(g26)
    c: Equal(g17,g14)
    c: Equal(g24,g26)
    c: Coincident(g16,g27)
    c: Coincident(g27,g28)
    c: Horizontal(g28)
    c: Coincident(g28,g29)
    c: Coincident(g29,g15)
    c: DistanceX(g27,g22) = 0
    c: DistanceY(g27,g22) = 5
    c: DistanceX(g28,g23) = 0
    c: Equal(g29,g27)
    c: DistanceX(g4,g14) = 0.4
    c: DistanceY(g14,g4) = 0.4
    c: Equal(g3,g7)
    c: DistanceX(g3,g3) = 26.2
    c: DistanceX(g17,g17) = 25
    c: DistanceY(g18,g1) = 15
FEATURE [PartDesign::Pad] Pad
  Direction = (0,-1,2e-16)
  Length = 25
  Length2 = 10
  Placement = pos=(0,0,0) rot=(1,0,0;1.5708rad)
  Profile = -> Sketch
  ReferenceAxis = -> Sketch [N_Axis]
  Refine = true
  Suppressed = false
  Type = 0
FEATURE [Sketcher::SketchObject] Sketch001
  ArcFitTolerance = 1e-06
  AttachmentSupport = -> [Pad]
  FullyConstrained = true
  MakeInternals = false
  MapMode = 5
  Placement = pos=(0,-1.2e-15,-5.4) rot=(0,0,1;3.14159rad)
  sketch-geometry (14):
    g0: LineSegment [constr] StartX=-65.4 StartY=0 StartZ=0 EndX=-40.4 EndY=0 EndZ=0
    g1: LineSegment [constr] StartX=-40.4 StartY=0 StartZ=0 EndX=-40.4 EndY=25 EndZ=0
    g2: LineSegment [constr] StartX=-40.4 StartY=25 StartZ=0 EndX=-65.4 EndY=25 EndZ=0
    g3: LineSegment [constr] StartX=-65.4 StartY=25 StartZ=0 EndX=-65.4 EndY=0 EndZ=0
    g4: LineSegment [constr] StartX=65.4 StartY=0 StartZ=0 EndX=65.4 EndY=25 EndZ=0
    g5: LineSegment [constr] StartX=65.4 StartY=25 StartZ=0 EndX=40.4 EndY=25 EndZ=0
    g6: LineSegment [constr] StartX=40.4 StartY=25 StartZ=0 EndX=40.4 EndY=0 EndZ=0
    g7: LineSegment [constr] StartX=40.4 StartY=0 StartZ=0 EndX=65.4 EndY=0 EndZ=0
    g8: LineSegment [constr] StartX=-65.4 StartY=25 StartZ=0 EndX=-40.4 EndY=0 EndZ=0
    g9: LineSegment [constr] StartX=-65.4 StartY=0 StartZ=0 EndX=-40.4 EndY=25 EndZ=0
    g10: LineSegment [constr] StartX=40.4 StartY=25 StartZ=0 EndX=65.4 EndY=0 EndZ=0
    g11: LineSegment [constr] StartX=40.4 StartY=0 StartZ=0 EndX=65.4 EndY=25 EndZ=0
    g12: Circle CenterX=-52.9 CenterY=12.5 CenterZ=0 NormalX=0 NormalY=0 NormalZ=1 AngleXU=0 Radius=4.3
    g13: Circle CenterX=52.9 CenterY=12.5 CenterZ=0 NormalX=0 NormalY=0 NormalZ=1 AngleXU=0 Radius=4.3
  constraints (36):
    c: Coincident(g0,g1)
    c: Coincident(g1,g2)
    c: Coincident(g2,g3)
    c: Coincident(g3,g0)
    c: Horizontal(g0)
    c: Horizontal(g2)
    c: Vertical(g1)
    c: Vertical(g3)
    c: Distance(g1,g3) = 25
    c: Distance(g0,g2) = 25
    c: PointOnObject(g0,g-1)
    c: DistanceX(g0) = -40.4
    c: Coincident(g4,g5)
    c: Coincident(g5,g6)
    c: Coincident(g6,g7)
    c: Coincident(g7,g4)
    c: Vertical(g4)
    c: Vertical(g6)
    c: Horizontal(g5)
    c: Horizontal(g7)
    c: PointOnObject(g4,g-1)
    c: Equal(g6,g5)
    c: Equal(g5,g1)
    c: DistanceX(g6) = 40.4
    c: Coincident(g8,g2)
    c: Coincident(g8,g0)
    c: Coincident(g9,g0)
    c: Coincident(g9,g1)
    c: Coincident(g10,g5)
    c: Coincident(g10,g4)
    c: Coincident(g11,g6)
    c: Coincident(g11,g4)
    c: Diameter(g12) = 8.6
    c: Symmetric(g8,g8,g12)
    c: Symmetric(g11,g11,g13)
    c: Equal(g13,g12)
FEATURE [PartDesign::Pocket] Pocket
  BaseFeature = -> Pad
  Direction = (0,0,-1)
  Length = 5
  Length2 = 5
  Placement = pos=(0,0,0) rot=(1,0,0;1.5708rad)
  Profile = -> Sketch001
  ReferenceAxis = -> Sketch001 [N_Axis]
  Refine = true
  Suppressed = false
  Type = 1
FEATURE [Sketcher::SketchObject] Sketch002
  ArcFitTolerance = 1e-06
  AttachmentOffset = pos=(0,0,-5) rot=(0,0,1;0rad)
  AttachmentSupport = -> [Pocket]
  FullyConstrained = true
  MakeInternals = false
  MapMode = 5
  Placement = pos=(0,-1.2e-15,-10.4) rot=(0,0,1;3.14159rad)
  expr: Constraints[11] = Sketch001.Constraints[11]
  expr: Constraints[23] = Sketch001.Constraints[23]
  expr: Constraints[32] = Sketch001.Constraints[32]
  expr: Constraints[8] = Sketch001.Constraints[8]
  expr: Constraints[9] = Sketch001.Constraints[9]
  sketch-geometry (28):
    g0: LineSegment [constr] StartX=-65.4 StartY=0 StartZ=0 EndX=-40.4 EndY=0 EndZ=0
    g1: LineSegment [constr] StartX=-40.4 StartY=0 StartZ=0 EndX=-40.4 EndY=25 EndZ=0
    g2: LineSegment [constr] StartX=-40.4 StartY=25 StartZ=0 EndX=-65.4 EndY=25 EndZ=0
    g3: LineSegment [constr] StartX=-65.4 StartY=25 StartZ=0 EndX=-65.4 EndY=0 EndZ=0
    g4: LineSegment [constr] StartX=65.4 StartY=0 StartZ=0 EndX=65.4 EndY=25 EndZ=0
    g5: LineSegment [constr] StartX=65.4 StartY=25 StartZ=0 EndX=40.4 EndY=25 EndZ=0
    g6: LineSegment [constr] StartX=40.4 StartY=25 StartZ=0 EndX=40.4 EndY=0 EndZ=0
    g7: LineSegment [constr] StartX=40.4 StartY=0 StartZ=0 EndX=65.4 EndY=0 EndZ=0
    g8: LineSegment [constr] StartX=-65.4 StartY=25 StartZ=0 EndX=-40.4 EndY=0 EndZ=0
    g9: LineSegment [constr] StartX=-65.4 StartY=0 StartZ=0 EndX=-40.4 EndY=25 EndZ=0
    g10: LineSegment [constr] StartX=40.4 StartY=25 StartZ=0 EndX=65.4 EndY=0 EndZ=0
    g11: LineSegment [constr] StartX=40.4 StartY=0 StartZ=0 EndX=65.4 EndY=25 EndZ=0
    g12: Circle [constr] CenterX=-52.9 CenterY=12.5 CenterZ=0 NormalX=0 NormalY=0 NormalZ=1 AngleXU=0 Radius=4.3
    g13: Circle [constr] CenterX=52.9 CenterY=12.5 CenterZ=0 NormalX=0 NormalY=0 NormalZ=1 AngleXU=0 Radius=4.3
    g14: LineSegment StartX=-46.3 StartY=8.68949 StartZ=0 EndX=-46.3 EndY=16.3105 EndZ=0
    g15: LineSegment StartX=-46.3 StartY=16.3105 StartZ=0 EndX=-52.9 EndY=20.121 EndZ=0
    g16: LineSegment StartX=-52.9 StartY=20.121 StartZ=0 EndX=-59.5 EndY=16.3105 EndZ=0
    g17: LineSegment StartX=-59.5 StartY=16.3105 StartZ=0 EndX=-59.5 EndY=8.68949 EndZ=0
    g18: LineSegment StartX=-59.5 StartY=8.68949 StartZ=0 EndX=-52.9 EndY=4.87898 EndZ=0
    g19: LineSegment StartX=-52.9 StartY=4.87898 StartZ=0 EndX=-46.3 EndY=8.68949 EndZ=0
    g20: Circle [constr] CenterX=-52.9 CenterY=12.5 CenterZ=0 NormalX=0 NormalY=0 NormalZ=1 AngleXU=0 Radius=7.62102
    g21: LineSegment StartX=59.5 StartY=8.68949 StartZ=0 EndX=59.5 EndY=16.3105 EndZ=0
    g22: LineSegment StartX=59.5 StartY=16.3105 StartZ=0 EndX=52.9 EndY=20.121 EndZ=0
    g23: LineSegment StartX=52.9 StartY=20.121 StartZ=0 EndX=46.3 EndY=16.3105 EndZ=0
    g24: LineSegment StartX=46.3 StartY=16.3105 StartZ=0 EndX=46.3 EndY=8.68949 EndZ=0
    g25: LineSegment StartX=46.3 StartY=8.68949 StartZ=0 EndX=52.9 EndY=4.87898 EndZ=0
    g26: LineSegment StartX=52.9 StartY=4.87898 StartZ=0 EndX=59.5 EndY=8.68949 EndZ=0
    g27: Circle [constr] CenterX=52.9 CenterY=12.5 CenterZ=0 NormalX=0 NormalY=0 NormalZ=1 AngleXU=0 Radius=7.62102
  constraints (68):
    c: Coincident(g0,g1)
    c: Coincident(g1,g2)
    c: Coincident(g2,g3)
    c: Coincident(g3,g0)
    c: Horizontal(g0)
    c: Horizontal(g2)
    c: Vertical(g1)
    c: Vertical(g3)
    c: Distance(g1,g3) = 25
    c: Distance(g0,g2) = 25
    c: PointOnObject(g0,g-1)
    c: DistanceX(g0) = -40.4
    c: Coincident(g4,g5)
    c: Coincident(g5,g6)
    c: Coincident(g6,g7)
    c: Coincident(g7,g4)
    c: Vertical(g4)
    c: Vertical(g6)
    c: Horizontal(g5)
    c: Horizontal(g7)
    c: PointOnObject(g4,g-1)
    c: Equal(g6,g5)
    c: Equal(g5,g1)
    c: DistanceX(g6) = 40.4
    c: Coincident(g8,g2)
    c: Coincident(g8,g0)
    c: Coincident(g9,g0)
    c: Coincident(g9,g1)
    c: Coincident(g10,g5)
    c: Coincident(g10,g4)
    c: Coincident(g11,g6)
    c: Coincident(g11,g4)
    c: Diameter(g12) = 8.6
    c: Symmetric(g8,g8,g12)
    c: Symmetric(g11,g11,g13)
    c: Equal(g13,g12)
    c: Coincident(g14,g15)
    c: Coincident(g15,g16)
    c: Coincident(g16,g17)
    c: Coincident(g17,g18)
    c: Coincident(g18,g19)
    c: Coincident(g19,g14)
    c: Equal(g14, g15-g19) x5
    c: PointOnObject(g14,g20)
    c: PointOnObject(g15,g20)
    c: PointOnObject(g16,g20)
    c: PointOnObject(g17,g20)
    c: PointOnObject(g18,g20)
    c: PointOnObject(g19,g20)
    c: Coincident(g20,g12)
    c: Vertical(g17)
    c: DistanceX(g16,g14) = 13.2
    c: Coincident(g21,g22)
    c: Coincident(g22,g23)
    c: Coincident(g23,g24)
    c: Coincident(g24,g25)
    c: Coincident(g25,g26)
    c: Coincident(g26,g21)
    c: Equal(g21, g22-g26) x5
    c: PointOnObject(g21,g27)
    c: PointOnObject(g22,g27)
    c: PointOnObject(g23,g27)
    c: PointOnObject(g24,g27)
    c: PointOnObject(g25,g27)
    c: PointOnObject(g26,g27)
    c: Coincident(g27,g13)
    c: Vertical(g21)
    c: Equal(g16,g23)
FEATURE [PartDesign::Pocket] Pocket001
  BaseFeature = -> Pocket
  Direction = (0,0,-1)
  Length = 5
  Length2 = 5
  Placement = pos=(0,0,0) rot=(1,0,0;1.5708rad)
  Profile = -> Sketch002
  ReferenceAxis = -> Sketch002 [N_Axis]
  Refine = true
  Suppressed = false
  Type = 1
FEATURE [PartDesign::Fillet] Fillet
  Base = -> Pocket001 [Edge25,Edge16,Edge21,Edge12]
  BaseFeature = -> Pocket001
  Placement = pos=(0,0,0) rot=(1,0,0;1.5708rad)
  Radius = 4
  Refine = true
  SupportTransform = false
  Suppressed = false
  UseAllEdges = false
FEATURE [PartDesign::Fillet] Fillet001
  Base = -> Fillet [Edge46,Edge38]
  BaseFeature = -> Fillet
  Placement = pos=(0,0,0) rot=(1,0,0;1.5708rad)
  Radius = 18
  Refine = true
  SupportTransform = false
  Suppressed = false
  UseAllEdges = false
FEATURE [PartDesign::Body] Body  label="sway_motor_mount_bottom"
  AllowCompound = false
  Group = -> [Sketch,Pad,Sketch001,Pocket,Sketch002,Pocket001,Fillet,Fillet001]
  Origin = -> Origin
  Tip = -> Fillet001
---- part sway_motor_mount_front_plate.FCStd = doc fcstd_8da22c537705 ----
FCSTD DOCUMENT  (FreeCAD 1.0R39109 (Git))
Label: sway_motor_mount_front_plate
License: All rights reserved
LicenseURL: https://en.wikipedia.org/wiki/All_rights_reserved
objects: Sketcher::SketchObject×4, PartDesign::Fillet×3, PartDesign::Pad×2, PartDesign::Pocket×2, PartDesign::Chamfer×1, PartDesign::Body×1
note: 33 computed .brp shape members not serialized (recipe doc carries the construction recipe); baked Part::Feature solids carry a one-line shape summary decoded from their .brp

FEATURE [Sketcher::SketchObject] Sketch
  ArcFitTolerance = 1e-06
  AttachmentSupport = -> [XY_Plane]
  FullyConstrained = false
  MakeInternals = false
  MapMode = 5
  sketch-geometry (17):
    g0: LineSegment [constr] StartX=0 StartY=0 StartZ=0 EndX=178 EndY=0 EndZ=0
    g1: LineSegment [constr] StartX=178 StartY=0 StartZ=0 EndX=178 EndY=70 EndZ=0
    g2: LineSegment [constr] StartX=178 StartY=70 StartZ=0 EndX=0 EndY=70 EndZ=0
    g3: LineSegment [constr] StartX=0 StartY=70 StartZ=0 EndX=0 EndY=0 EndZ=0
    g4: Circle CenterX=15 CenterY=60 CenterZ=0 NormalX=0 NormalY=0 NormalZ=1 AngleXU=0 Radius=4.3
    g5: Circle CenterX=15 CenterY=10 CenterZ=0 NormalX=0 NormalY=0 NormalZ=1 AngleXU=0 Radius=4.3
    g6: LineSegment StartX=0.4 StartY=70 StartZ=0 EndX=0.4 EndY=-0.4 EndZ=0
    g7: LineSegment [constr] StartX=-19 StartY=-27 StartZ=0 EndX=-19 EndY=-107 EndZ=0
    g8: LineSegment [constr] StartX=-19 StartY=-107 StartZ=0 EndX=95.6 EndY=-107 EndZ=0
    g9: LineSegment [constr] StartX=95.6 StartY=-107 StartZ=0 EndX=95.6 EndY=-27 EndZ=0
    g10: LineSegment [constr] StartX=95.6 StartY=-27 StartZ=0 EndX=-19 EndY=-27 EndZ=0
    g11: LineSegment StartX=0.4 StartY=-0.4 StartZ=0 EndX=-19 EndY=-0.4 EndZ=0
    g12: LineSegment StartX=-19 StartY=-0.4 StartZ=0 EndX=-19 EndY=-26.6 EndZ=0
    g13: LineSegment StartX=-19 StartY=-26.6 StartZ=0 EndX=115.6 EndY=-26.6 EndZ=0
    g14: LineSegment StartX=115.6 StartY=-26.6 StartZ=0 EndX=115.6 EndY=0 EndZ=0
    g15: LineSegment StartX=115.6 StartY=0 StartZ=0 EndX=115.6 EndY=70 EndZ=0
    g16: LineSegment StartX=115.6 StartY=70 StartZ=0 EndX=0.4 EndY=70 EndZ=0
  constraints (49):
    c: Coincident(g0,g1)
    c: Coincident(g1,g2)
    c: Coincident(g2,g3)
    c: Coincident(g3,g0)
    c: Horizontal(g0)
    c: Horizontal(g2)
    c: Vertical(g1)
    c: Vertical(g3)
    c: Distance(g0,g2) = 70
    c: Coincident(g0,g-1)
    c: DistanceX(g5) = 15
    c: DistanceX(g5,g4) = 0
    c: DistanceY(g5,g4) = 50
    c: Equal(g5,g4)
    c: Diameter(g5) = 8.6
    c: DistanceY(g0,g5) = 10
    c: Vertical(g6)
    c: DistanceX(g6) = 0.4
    c: Coincident(g7,g8)
    c: Coincident(g8,g9)
    c: Coincident(g9,g10)
    c: Coincident(g10,g7)
    c: Vertical(g7)
    c: Vertical(g9)
    c: Horizontal(g8)
    c: Horizontal(g10)
    c: DistanceX(g8,g8) = 114.6
    c: DistanceY(g7,g7) = 80
    c: DistanceX(g7) = -19
    c: DistanceY(g7) = -27
    c: PointOnObject(g6,g2)
    c: DistanceY(g6,g0) = 0.4
    c: Coincident(g6,g11)
    c: Horizontal(g11)
    c: Coincident(g11,g12)
    c: Vertical(g12)
    c: Coincident(g12,g13)
    c: Horizontal(g13)
    c: Coincident(g13,g14)
    c: PointOnObject(g14,g0)
    c: Coincident(g14,g15)
    c: PointOnObject(g15,g2)
    c: Vertical(g15)
    c: Coincident(g15,g16)
    c: Coincident(g16,g6)
    c: DistanceY(g7,g12) = 0.4
    c: DistanceX(g12,g7) = 0
    c: DistanceX(g9,g13) = 20
    c: Vertical(g14)
FEATURE [PartDesign::Pad] Pad
  Direction = (0,0,1)
  Length = 10
  Length2 = 10
  Profile = -> Sketch
  ReferenceAxis = -> Sketch [N_Axis]
  Refine = true
  Suppressed = false
  Type = 0
FEATURE [Sketcher::SketchObject] Sketch001
  ArcFitTolerance = 1e-06
  AttachmentSupport = -> [Pad]
  FullyConstrained = true
  MakeInternals = false
  MapMode = 5
  Placement = pos=(0,-26.6,0) rot=(1,0,0;1.5708rad)
  sketch-geometry (14):
    g0: LineSegment StartX=115.6 StartY=0 StartZ=0 EndX=178 EndY=35 EndZ=0
    g1: LineSegment StartX=178 StartY=35 StartZ=0 EndX=202 EndY=35 EndZ=0
    g2: LineSegment StartX=202 StartY=35 StartZ=0 EndX=202 EndY=45 EndZ=0
    g3: LineSegment StartX=202 StartY=45 StartZ=0 EndX=178 EndY=45 EndZ=0
    g4: LineSegment StartX=178 StartY=45 StartZ=0 EndX=115.6 EndY=10 EndZ=0
    g5: LineSegment StartX=115.6 StartY=10 StartZ=0 EndX=115.6 EndY=0 EndZ=0
    g6: LineSegment [constr] StartX=115.6 StartY=0 StartZ=0 EndX=123.25 EndY=0 EndZ=0
    g7: LineSegment [constr] StartX=123.25 StartY=0 StartZ=0 EndX=123.25 EndY=-1.1 EndZ=0
    g8: LineSegment [constr] StartX=118.25 StartY=-1.1 StartZ=0 EndX=118.25 EndY=-11.1 EndZ=0
    g9: LineSegment [constr] StartX=118.25 StartY=-11.1 StartZ=0 EndX=128.25 EndY=-11.1 EndZ=0
    g10: LineSegment [constr] StartX=128.25 StartY=-11.1 StartZ=0 EndX=128.25 EndY=-1.1 EndZ=0
    g11: LineSegment [constr] StartX=128.25 StartY=-1.1 StartZ=0 EndX=118.25 EndY=-1.1 EndZ=0
    g12: LineSegment [constr] StartX=118.25 StartY=-6.1 StartZ=0 EndX=128.25 EndY=-6.1 EndZ=0
    g13: LineSegment [constr] StartX=123.25 StartY=-6.1 StartZ=0 EndX=123.25 EndY=2.9 EndZ=0
  constraints (43):
    c: PointOnObject(g0,g-1)
    c: Coincident(g0,g1)
    c: Horizontal(g1)
    c: Coincident(g1,g2)
    c: Vertical(g2)
    c: Coincident(g2,g3)
    c: Horizontal(g3)
    c: Coincident(g3,g4)
    c: Coincident(g4,g5)
    c: Coincident(g5,g0)
    c: Vertical(g5)
    c: DistanceY(g2,g2) = 10
    c: DistanceX(g0) = 115.6
    c: DistanceX(g0,g1) = 86.4
    c: DistanceX(g1,g1) = 24
    c: Equal(g1,g3)
    c: Coincident(g6,g0)
    c: Horizontal(g6)
    c: DistanceX(g6,g6) = 7.65
    c: Coincident(g7,g6)
    c: Vertical(g7)
    c: DistanceY(g7) = -1.1
    c: Coincident(g8,g9)
    c: Coincident(g9,g10)
    c: Coincident(g10,g11)
    c: Coincident(g11,g8)
    c: Vertical(g8)
    c: Vertical(g10)
    c: Horizontal(g9)
    c: Horizontal(g11)
    c: PointOnObject(g7,g11)
    c: DistanceY(g10,g10) = 10
    c: Equal(g8,g11)
    c: DistanceX(g8,g7) = 5
    c: PointOnObject(g12,g8)
    c: PointOnObject(g12,g10)
    c: Horizontal(g12)
    c: DistanceY(g12,g8) = 5
    c: Symmetric(g12,g12,g13)
    c: Vertical(g13)
    c: DistanceY(g13,g13) = 9
    c: DistanceY(g4,g1) = 25
    c: DistanceY(g5,g5) = 10
FEATURE [PartDesign::Pad] Pad001
  BaseFeature = -> Pad
  Direction = (0,-1,2e-16)
  Length = 23
  Length2 = 10
  Profile = -> Sketch001
  ReferenceAxis = -> Sketch001 [N_Axis]
  Refine = true
  Reversed = true
  Suppressed = false
  Type = 0
FEATURE [PartDesign::Fillet] Fillet
  Base = -> Pad001 [Edge23]
  BaseFeature = -> Pad001
  Radius = 17
  Refine = true
  SupportTransform = false
  Suppressed = false
  UseAllEdges = false
FEATURE [Sketcher::SketchObject] Sketch002
  ArcFitTolerance = 1e-06
  AttachmentSupport = -> [Fillet]
  FullyConstrained = true
  MakeInternals = false
  MapMode = 5
  Placement = pos=(0,9.9e-15,45) rot=(0,0,1;0rad)
  sketch-geometry (7):
    g0: LineSegment [constr] StartX=202 StartY=-26.6 StartZ=0 EndX=202 EndY=-3.6 EndZ=0
    g1: LineSegment [constr] StartX=202 StartY=-3.6 StartZ=0 EndX=178 EndY=-3.6 EndZ=0
    g2: LineSegment [constr] StartX=178 StartY=-3.6 StartZ=0 EndX=178 EndY=-26.6 EndZ=0
    g3: LineSegment [constr] StartX=178 StartY=-26.6 StartZ=0 EndX=202 EndY=-26.6 EndZ=0
    g4: LineSegment [constr] StartX=178 StartY=-26.6 StartZ=0 EndX=202 EndY=-3.6 EndZ=0
    g5: LineSegment [constr] StartX=178 StartY=-3.6 StartZ=0 EndX=202 EndY=-26.6 EndZ=0
    g6: Circle CenterX=190 CenterY=-15.1 CenterZ=0 NormalX=0 NormalY=0 NormalZ=1 AngleXU=0 Radius=4.3
  constraints (18):
    c: Coincident(g0,g1)
    c: Coincident(g1,g2)
    c: Coincident(g2,g3)
    c: Coincident(g3,g0)
    c: Vertical(g0)
    c: Vertical(g2)
    c: Horizontal(g1)
    c: Horizontal(g3)
    c: Distance(g0,g2) = 24
    c: Distance(g1,g3) = 23
    c: DistanceY(g0) = -3.6
    c: DistanceX(g0) = 202
    c: Coincident(g4,g2)
    c: Coincident(g4,g0)
    c: Coincident(g5,g1)
    c: Coincident(g5,g0)
    c: Diameter(g6) = 8.6
    c: Symmetric(g4,g4,g6)
FEATURE [PartDesign::Pocket] Pocket
  BaseFeature = -> Fillet
  Direction = (0,0,-1)
  Length = 5
  Length2 = 5
  Profile = -> Sketch002
  ReferenceAxis = -> Sketch002 [N_Axis]
  Refine = true
  Suppressed = false
  Type = 1
FEATURE [PartDesign::Fillet] Fillet001
  Base = -> Pocket [Edge24]
  BaseFeature = -> Pocket
  Radius = 4
  Refine = true
  SupportTransform = false
  Suppressed = false
  UseAllEdges = false
FEATURE [Sketcher::SketchObject] Sketch003
  ArcFitTolerance = 1e-06
  AttachmentSupport = -> [Fillet001]
  FullyConstrained = true
  MakeInternals = false
  MapMode = 5
  Placement = pos=(0,0,10) rot=(0,0,1;0rad)
  sketch-geometry (19):
    g0: LineSegment [constr] StartX=-19 StartY=-26.6 StartZ=0 EndX=-19 EndY=-106.6 EndZ=0
    g1: LineSegment [constr] StartX=-19 StartY=-106.6 StartZ=0 EndX=95.6 EndY=-106.6 EndZ=0
    g2: LineSegment [constr] StartX=95.6 StartY=-106.6 StartZ=0 EndX=95.6 EndY=-26.6 EndZ=0
    g3: LineSegment [constr] StartX=95.6 StartY=-26.6 StartZ=0 EndX=-19 EndY=-26.6 EndZ=0
    g4: LineSegment [constr] StartX=-19 StartY=-26.6 StartZ=0 EndX=-19 EndY=-1.6 EndZ=0
    g5: LineSegment [constr] StartX=-19 StartY=-1.6 StartZ=0 EndX=95.6 EndY=-1.6 EndZ=0
    g6: LineSegment [constr] StartX=95.6 StartY=-1.6 StartZ=0 EndX=95.6 EndY=-26.6 EndZ=0
    g7: LineSegment [constr] StartX=-4 StartY=-1.6 StartZ=0 EndX=-4 EndY=-26.6 EndZ=0
    g8: LineSegment [constr] StartX=-19 StartY=-1.6 StartZ=0 EndX=-4 EndY=-26.6 EndZ=0
    g9: LineSegment [constr] StartX=95.6 StartY=-1.6 StartZ=0 EndX=110.6 EndY=-1.6 EndZ=0
    g10: LineSegment [constr] StartX=110.6 StartY=-1.6 StartZ=0 EndX=110.6 EndY=-26.6 EndZ=0
    g11: LineSegment [constr] StartX=110.6 StartY=-26.6 StartZ=0 EndX=95.6 EndY=-26.6 EndZ=0
    g12: LineSegment [constr] StartX=11 StartY=-1.6 StartZ=0 EndX=11 EndY=-26.6 EndZ=0
    g13: LineSegment [constr] StartX=36 StartY=-1.6 StartZ=0 EndX=36 EndY=-26.6 EndZ=0
    g14: LineSegment [constr] StartX=11 StartY=-1.6 StartZ=0 EndX=36 EndY=-26.6 EndZ=0
    g15: LineSegment [constr] StartX=95.6 StartY=-1.6 StartZ=0 EndX=110.6 EndY=-26.6 EndZ=0
    g16: Circle CenterX=-11.5 CenterY=-14.1 CenterZ=0 NormalX=0 NormalY=0 NormalZ=1 AngleXU=0 Radius=4.3
    g17: Circle CenterX=23.5 CenterY=-14.1 CenterZ=0 NormalX=0 NormalY=0 NormalZ=1 AngleXU=0 Radius=4.3
    g18: Circle CenterX=103.1 CenterY=-14.1 CenterZ=0 NormalX=0 NormalY=0 NormalZ=1 AngleXU=0 Radius=4.3
  constraints (52):
    c: Coincident(g0,g1)
    c: Coincident(g1,g2)
    c: Coincident(g2,g3)
    c: Coincident(g3,g0)
    c: Vertical(g0)
    c: Vertical(g2)
    c: Horizontal(g1)
    c: Horizontal(g3)
    c: DistanceY(g0) = -26.6
    c: DistanceX(g0,g-1) = 19
    c: DistanceX(g3,g3) = 114.6
    c: DistanceY(g0,g0) = 80
    c: Coincident(g0,g4)
    c: Vertical(g4)
    c: Coincident(g4,g5)
    c: Horizontal(g5)
    c: Coincident(g5,g6)
    c: Coincident(g6,g2)
    c: Vertical(g6)
    c: DistanceY(g4,g4) = 25
    c: PointOnObject(g7,g5)
    c: PointOnObject(g7,g3)
    c: Vertical(g7)
    c: DistanceX(g4,g7) = 15
    c: Coincident(g8,g4)
    c: Coincident(g8,g7)
    c: Coincident(g5,g9)
    c: Horizontal(g9)
    c: Coincident(g9,g10)
    c: Vertical(g10)
    c: Coincident(g10,g11)
    c: Coincident(g11,g2)
    c: Horizontal(g11)
    c: DistanceX(g9,g9) = 15
    c: PointOnObject(g12,g5)
    c: PointOnObject(g12,g3)
    c: Vertical(g12)
    c: PointOnObject(g13,g5)
    c: PointOnObject(g13,g3)
    c: Vertical(g13)
    c: DistanceX(g12,g13) = 25
    c: DistanceX(g4,g12) = 30
    c: Coincident(g14,g12)
    c: Coincident(g14,g13)
    c: Coincident(g15,g5)
    c: Coincident(g15,g10)
    c: Diameter(g16) = 8.6
    c: Symmetric(g8,g8,g16)
    c: Symmetric(g14,g14,g17)
    c: Symmetric(g15,g15,g18)
    c: Equal(g16,g17)
    c: Equal(g17,g18)
FEATURE [PartDesign::Pocket] Pocket001
  BaseFeature = -> Fillet001
  Direction = (0,0,-1)
  Length = 5
  Length2 = 5
  Profile = -> Sketch003
  ReferenceAxis = -> Sketch003 [N_Axis]
  Refine = true
  Suppressed = false
  Type = 1
FEATURE [PartDesign::Chamfer] Chamfer
  Angle = 45
  Base = -> Pocket001 [Edge53]
  BaseFeature = -> Pocket001
  ChamferType = 1
  FlipDirection = false
  Refine = true
  Size = 50
  Size2 = 80
  SupportTransform = false
  Suppressed = false
  UseAllEdges = false
FEATURE [PartDesign::Fillet] Fillet002
  Base = -> Chamfer [Edge16,Edge18]
  BaseFeature = -> Chamfer
  Radius = 11.9
  Refine = true
  SupportTransform = false
  Suppressed = false
  UseAllEdges = false
FEATURE [PartDesign::Body] Body  label="sway_motor_mount_front_plate"
  AllowCompound = false
  Group = -> [Sketch,Pad,Sketch001,Pad001,Fillet,Sketch002,Pocket,Fillet001,Sketch003,Pocket001,Chamfer,Fillet002]
  Origin = -> Origin
  Tip = -> Fillet002
---- part sway_motor_mount_front_plate_shaft_support.FCStd = doc fcstd_e6d54d698b7d ----
FCSTD DOCUMENT  (FreeCAD 1.0R39109 (Git))
Label: sway_motor_mount_front_plate_shaft_support
License: All rights reserved
LicenseURL: https://en.wikipedia.org/wiki/All_rights_reserved
objects: Sketcher::SketchObject×3, PartDesign::Pocket×2, PartDesign::Fillet×2, PartDesign::Pad×1, PartDesign::Body×1
note: 22 computed .brp shape members not serialized (recipe doc carries the construction recipe); baked Part::Feature solids carry a one-line shape summary decoded from their .brp

FEATURE [Sketcher::SketchObject] Sketch
  ArcFitTolerance = 1e-06
  AttachmentSupport = -> [YZ_Plane]
  FullyConstrained = true
  MakeInternals = false
  MapMode = 5
  Placement = pos=(0,0,0) rot=(0.57735,0.57735,0.57735;2.0944rad)
  sketch-geometry (17):
    g0: ArcOfCircle [constr] CenterX=0 CenterY=0 CenterZ=0 NormalX=0 NormalY=0 NormalZ=1 AngleXU=0 Radius=12.9 StartAngle=3.5735 EndAngle=8.99287
    g1: ArcOfCircle CenterX=0 CenterY=0 CenterZ=0 NormalX=0 NormalY=0 NormalZ=1 AngleXU=0 Radius=20.9 StartAngle=3.83759 EndAngle=8.72878
    g2: LineSegment [constr] StartX=-11.7154 StartY=5.4 StartZ=0 EndX=-38.6 EndY=5.4 EndZ=0
    g3: LineSegment StartX=-61.6 StartY=13.4 StartZ=0 EndX=-16.039 EndY=13.4 EndZ=0
    g4: LineSegment [constr] StartX=-11.7154 StartY=-5.4 StartZ=0 EndX=-38.6 EndY=-5.4 EndZ=0
    g5: LineSegment StartX=-61.6 StartY=-13.4 StartZ=0 EndX=-16.039 EndY=-13.4 EndZ=0
    g6: Circle [constr] CenterX=0 CenterY=0 CenterZ=0 NormalX=0 NormalY=0 NormalZ=1 AngleXU=0 Radius=12.5
    g7: LineSegment [constr] StartX=-12.5 StartY=0 StartZ=0 EndX=-38.6 EndY=0 EndZ=0
    g8: LineSegment StartX=-61.6 StartY=13.4 StartZ=0 EndX=-61.6 EndY=5.4 EndZ=0
    g9: LineSegment StartX=-61.6 StartY=5.4 StartZ=0 EndX=-38.2 EndY=5.4 EndZ=0
    g10: LineSegment StartX=-61.6 StartY=-13.4 StartZ=0 EndX=-61.6 EndY=-5.4 EndZ=0
    g11: LineSegment StartX=-61.6 StartY=-5.4 StartZ=0 EndX=-38.2 EndY=-5.4 EndZ=0
    g12: ArcOfCircle CenterX=0 CenterY=0 CenterZ=0 NormalX=0 NormalY=0 NormalZ=1 AngleXU=0 Radius=12.9 StartAngle=3.29726 EndAngle=9.26911
    g13: LineSegment StartX=-38.2 StartY=5.4 StartZ=0 EndX=-38.2 EndY=2 EndZ=0
    g14: LineSegment StartX=-38.2 StartY=2 StartZ=0 EndX=-12.744 EndY=2 EndZ=0
    g15: LineSegment StartX=-38.2 StartY=-5.4 StartZ=0 EndX=-38.2 EndY=-2 EndZ=0
    g16: LineSegment StartX=-38.2 StartY=-2 StartZ=0 EndX=-12.744 EndY=-2 EndZ=0
  constraints (52):
    c: Coincident(g0,g-1)
    c: Coincident(g1,g0)
    c: Diameter(g0) = 25.8
    c: Coincident(g2,g0)
    c: Horizontal(g2)
    c: Coincident(g3,g1)
    c: Coincident(g4,g0)
    c: Horizontal(g4)
    c: Coincident(g5,g1)
    c: Horizontal(g3)
    c: Horizontal(g5)
    c: Equal(g5,g3)
    c: Equal(g4,g2)
    c: DistanceY(g4,g2) = 10.8
    c: DistanceY(g5,g4) = 8
    c: Diameter(g1) = 41.8
    c: Coincident(g6,g0)
    c: Diameter(g6) = 25
    c: PointOnObject(g7,g6)
    c: PointOnObject(g7,g-1)
    c: Horizontal(g7)
    c: DistanceX(g7,g7) = 26.1
    c: DistanceX(g2,g7) = 0
    c: DistanceX(g2,g4) = 0
    c: DistanceX(g3,g2) = 23
    c: DistanceX(g3,g5) = 0
    c: Coincident(g3,g8)
    c: Vertical(g8)
    c: Coincident(g8,g9)
    c: PointOnObject(g9,g2)
    c: Horizontal(g9)
    c: Coincident(g5,g10)
    c: Vertical(g10)
    c: Coincident(g10,g11)
    c: PointOnObject(g11,g4)
    c: Horizontal(g11)
    c: DistanceX(g4,g11) = 0.4
    c: Equal(g11,g9)
    c: Coincident(g12,g0)
    c: PointOnObject(g12,g0)
    c: Coincident(g9,g13)
    c: Vertical(g13)
    c: Coincident(g13,g14)
    c: Coincident(g14,g12)
    c: Coincident(g11,g15)
    c: Vertical(g15)
    c: Coincident(g15,g16)
    c: Coincident(g16,g12)
    c: Horizontal(g16)
    c: Horizontal(g14)
    c: Equal(g13,g15)
    c: DistanceY(g15,g13) = 4
FEATURE [PartDesign::Pad] Pad
  Direction = (1,0,0)
  Length = 24
  Length2 = 10
  Placement = pos=(0,0,0) rot=(1,1,1;2.0944rad)
  Profile = -> Sketch
  ReferenceAxis = -> Sketch [N_Axis]
  Refine = true
  Suppressed = false
  Type = 0
FEATURE [Sketcher::SketchObject] Sketch001
  ArcFitTolerance = 1e-06
  AttachmentSupport = -> [Pad]
  FullyConstrained = true
  MakeInternals = false
  MapMode = 5
  Placement = pos=(-1.5e-15,4.5e-15,13.4) rot=(0,0,-1;1.5708rad)
  sketch-geometry (8):
    g0: LineSegment [constr] StartX=61.6 StartY=0 StartZ=0 EndX=61.6 EndY=24 EndZ=0
    g1: LineSegment [constr] StartX=61.6 StartY=24 StartZ=0 EndX=38.6 EndY=24 EndZ=0
    g2: LineSegment [constr] StartX=38.6 StartY=24 StartZ=0 EndX=38.6 EndY=0 EndZ=0
    g3: LineSegment [constr] StartX=38.6 StartY=0 StartZ=0 EndX=61.6 EndY=0 EndZ=0
    g4: LineSegment [constr] StartX=38.6 StartY=0 StartZ=0 EndX=61.6 EndY=24 EndZ=0
    g5: LineSegment [constr] StartX=38.6 StartY=24 StartZ=0 EndX=61.6 EndY=0 EndZ=0
    g6: Circle CenterX=50.1 CenterY=12 CenterZ=0 NormalX=0 NormalY=0 NormalZ=1 AngleXU=0 Radius=4.3
    g7: Circle CenterX=27.1 CenterY=12 CenterZ=0 NormalX=0 NormalY=0 NormalZ=1 AngleXU=0 Radius=4.3
  constraints (21):
    c: Coincident(g0,g1)
    c: Coincident(g1,g2)
    c: Coincident(g2,g3)
    c: Coincident(g3,g0)
    c: Vertical(g0)
    c: Vertical(g2)
    c: Horizontal(g1)
    c: Horizontal(g3)
    c: Distance(g0,g2) = 23
    c: Distance(g1,g3) = 24
    c: PointOnObject(g0,g-1)
    c: DistanceX(g0) = 61.6
    c: Coincident(g4,g2)
    c: Coincident(g4,g0)
    c: Coincident(g5,g1)
    c: Coincident(g5,g0)
    c: Diameter(g6) = 8.6
    c: Symmetric(g4,g4,g6)
    c: Equal(g6,g7)
    c: DistanceY(g7,g6) = 0
    c: DistanceX(g7,g6) = 23
FEATURE [PartDesign::Pocket] Pocket
  BaseFeature = -> Pad
  Direction = (0,0,-1)
  Length = 5
  Length2 = 5
  Placement = pos=(0,0,0) rot=(1,1,1;2.0944rad)
  Profile = -> Sketch001
  ReferenceAxis = -> Sketch001 [N_Axis]
  Refine = true
  Suppressed = false
  Type = 1
FEATURE [Sketcher::SketchObject] Sketch002
  ArcFitTolerance = 1e-06
  AttachmentSupport = -> [Pocket]
  FullyConstrained = true
  MakeInternals = false
  MapMode = 5
  Placement = pos=(6e-15,-6e-15,-13.4) rot=(0.707107,0.707107,0;3.14159rad)
  sketch-geometry (16):
    g0: Circle [constr] CenterX=-50.1 CenterY=12 CenterZ=0 NormalX=0 NormalY=0 NormalZ=1 AngleXU=0 Radius=4.3
    g1: Circle [constr] CenterX=-27.1 CenterY=12 CenterZ=0 NormalX=0 NormalY=0 NormalZ=1 AngleXU=0 Radius=4.3
    g2: LineSegment StartX=-43.5 StartY=8.18949 StartZ=0 EndX=-43.5 EndY=15.8105 EndZ=0
    g3: LineSegment StartX=-43.5 StartY=15.8105 StartZ=0 EndX=-50.1 EndY=19.621 EndZ=0
    g4: LineSegment StartX=-50.1 StartY=19.621 StartZ=0 EndX=-56.7 EndY=15.8105 EndZ=0
    g5: LineSegment StartX=-56.7 StartY=15.8105 StartZ=0 EndX=-56.7 EndY=8.18949 EndZ=0
    g6: LineSegment StartX=-56.7 StartY=8.18949 StartZ=0 EndX=-50.1 EndY=4.37898 EndZ=0
    g7: LineSegment StartX=-50.1 StartY=4.37898 StartZ=0 EndX=-43.5 EndY=8.18949 EndZ=0
    g8: Circle [constr] CenterX=-50.1 CenterY=12 CenterZ=0 NormalX=0 NormalY=0 NormalZ=1 AngleXU=0 Radius=7.62102
    g9: LineSegment StartX=-20.5 StartY=8.18949 StartZ=0 EndX=-20.5 EndY=15.8105 EndZ=0
    g10: LineSegment StartX=-20.5 StartY=15.8105 StartZ=0 EndX=-27.1 EndY=19.621 EndZ=0
    g11: LineSegment StartX=-27.1 StartY=19.621 StartZ=0 EndX=-33.7 EndY=15.8105 EndZ=0
    g12: LineSegment StartX=-33.7 StartY=15.8105 StartZ=0 EndX=-33.7 EndY=8.18949 EndZ=0
    g13: LineSegment StartX=-33.7 StartY=8.18949 StartZ=0 EndX=-27.1 EndY=4.37898 EndZ=0
    g14: LineSegment StartX=-27.1 StartY=4.37898 StartZ=0 EndX=-20.5 EndY=8.18949 EndZ=0
    g15: Circle [constr] CenterX=-27.1 CenterY=12 CenterZ=0 NormalX=0 NormalY=0 NormalZ=1 AngleXU=0 Radius=7.62102
  constraints (38):
    c: Diameter(g0) = 8.6
    c: DistanceY(g0) = 12
    c: DistanceX(g0) = -50.1
    c: Equal(g1,g0)
    c: DistanceX(g0,g1) = 23
    c: DistanceY(g0,g1) = 0
    c: Coincident(g2,g3)
    c: Coincident(g3,g4)
    c: Coincident(g4,g5)
    c: Coincident(g5,g6)
    c: Coincident(g6,g7)
    c: Coincident(g7,g2)
    c: Equal(g2, g3-g7) x5
    c: PointOnObject(g2,g8)
    c: PointOnObject(g3,g8)
    c: PointOnObject(g4,g8)
    c: PointOnObject(g5,g8)
    c: PointOnObject(g6,g8)
    c: PointOnObject(g7,g8)
    c: Coincident(g8,g0)
    c: Coincident(g9,g10)
    c: Coincident(g10,g11)
    c: Coincident(g11,g12)
    c: Coincident(g12,g13)
    c: Coincident(g13,g14)
    c: Coincident(g14,g9)
    c: Equal(g9, g10-g14) x5
    c: PointOnObject(g9,g15)
    c: PointOnObject(g10,g15)
    c: PointOnObject(g11,g15)
    c: PointOnObject(g12,g15)
    c: PointOnObject(g13,g15)
    c: PointOnObject(g14,g15)
    c: Coincident(g15,g1)
    c: Vertical(g5)
    c: Vertical(g12)
    c: DistanceX(g4,g2) = 13.2
    c: Equal(g11,g4)
FEATURE [PartDesign::Pocket] Pocket001
  BaseFeature = -> Pocket
  Direction = (0,0,1)
  Length = 5
  Length2 = 5
  Placement = pos=(0,0,0) rot=(1,1,1;2.0944rad)
  Profile = -> Sketch002
  ReferenceAxis = -> Sketch002 [N_Axis]
  Refine = true
  Suppressed = false
  Type = 0
FEATURE [PartDesign::Fillet] Fillet
  Base = -> Pocket001 [Edge32,Edge45,Edge12,Edge22,Edge7,Edge8]
  BaseFeature = -> Pocket001
  Placement = pos=(0,0,0) rot=(1,1,1;2.0944rad)
  Radius = 4
  Refine = true
  SupportTransform = false
  Suppressed = false
  UseAllEdges = false
FEATURE [PartDesign::Fillet] Fillet001
  Base = -> Fillet [Edge16]
  BaseFeature = -> Fillet
  Placement = pos=(0,0,0) rot=(1,1,1;2.0944rad)
  Radius = 2
  Refine = true
  SupportTransform = false
  Suppressed = false
  UseAllEdges = false
FEATURE [PartDesign::Body] Body  label="sway_motor_mount_front_plate_shaft_support"
  AllowCompound = false
  Group = -> [Sketch,Pad,Sketch001,Pocket,Sketch002,Pocket001,Fillet,Fillet001]
  Origin = -> Origin
  Tip = -> Fillet001
---- part sway_motor_mount_rear_plate.FCStd = doc fcstd_f9e0d7bb8d73 ----
FCSTD DOCUMENT  (FreeCAD 1.0R39109 (Git))
Label: sway_motor_mount_rear_plate
License: All rights reserved
LicenseURL: https://en.wikipedia.org/wiki/All_rights_reserved
objects: Sketcher::SketchObject×3, PartDesign::Pocket×2, PartDesign::Pad×1, PartDesign::Fillet×1, PartDesign::Body×1
note: 19 computed .brp shape members not serialized (recipe doc carries the construction recipe); baked Part::Feature solids carry a one-line shape summary decoded from their .brp

FEATURE [Sketcher::SketchObject] Sketch
  ArcFitTolerance = 1e-06
  AttachmentSupport = -> [XY_Plane]
  FullyConstrained = true
  MakeInternals = false
  MapMode = 5
  sketch-geometry (20):
    g0: LineSegment [constr] StartX=0 StartY=0 StartZ=0 EndX=178 EndY=0 EndZ=0
    g1: LineSegment [constr] StartX=178 StartY=0 StartZ=0 EndX=178 EndY=70 EndZ=0
    g2: LineSegment [constr] StartX=178 StartY=70 StartZ=0 EndX=0 EndY=70 EndZ=0
    g3: LineSegment [constr] StartX=0 StartY=70 StartZ=0 EndX=0 EndY=0 EndZ=0
    g4: Circle CenterX=15 CenterY=60 CenterZ=0 NormalX=0 NormalY=0 NormalZ=1 AngleXU=0 Radius=4.3
    g5: Circle CenterX=15 CenterY=10 CenterZ=0 NormalX=0 NormalY=0 NormalZ=1 AngleXU=0 Radius=4.3
    g6: Circle CenterX=170 CenterY=47 CenterZ=0 NormalX=0 NormalY=0 NormalZ=1 AngleXU=0 Radius=2.8
    g7: Circle CenterX=170 CenterY=23 CenterZ=0 NormalX=0 NormalY=0 NormalZ=1 AngleXU=0 Radius=2.8
    g8: LineSegment StartX=0.4 StartY=0 StartZ=0 EndX=177.6 EndY=0 EndZ=0
    g9: LineSegment StartX=177.6 StartY=0 StartZ=0 EndX=177.6 EndY=70 EndZ=0
    g10: LineSegment StartX=0.4 StartY=70.4 StartZ=0 EndX=0.4 EndY=0 EndZ=0
    g11: LineSegment [constr] StartX=-19 StartY=97 StartZ=0 EndX=95.6 EndY=97 EndZ=0
    g12: LineSegment [constr] StartX=95.6 StartY=97 StartZ=0 EndX=95.6 EndY=177 EndZ=0
    g13: LineSegment [constr] StartX=95.6 StartY=177 StartZ=0 EndX=-19 EndY=177 EndZ=0
    g14: LineSegment [constr] StartX=-19 StartY=177 StartZ=0 EndX=-19 EndY=97 EndZ=0
    g15: LineSegment StartX=0.4 StartY=70.4 StartZ=0 EndX=-19 EndY=70.4 EndZ=0
    g16: LineSegment StartX=-19 StartY=70.4 StartZ=0 EndX=-19 EndY=96.6 EndZ=0
    g17: LineSegment StartX=-19 StartY=96.6 StartZ=0 EndX=115.6 EndY=96.6 EndZ=0
    g18: LineSegment StartX=115.6 StartY=96.6 StartZ=0 EndX=115.6 EndY=70 EndZ=0
    g19: LineSegment StartX=115.6 StartY=70 StartZ=0 EndX=177.6 EndY=70 EndZ=0
  constraints (59):
    c: Coincident(g0,g1)
    c: Coincident(g1,g2)
    c: Coincident(g2,g3)
    c: Coincident(g3,g0)
    c: Horizontal(g0)
    c: Horizontal(g2)
    c: Vertical(g1)
    c: Vertical(g3)
    c: Distance(g1,g3) = 178
    c: Distance(g0,g2) = 70
    c: Coincident(g0,g-1)
    c: DistanceX(g5) = 15
    c: DistanceX(g5,g4) = 0
    c: DistanceY(g5,g4) = 50
    c: Equal(g5,g4)
    c: Diameter(g5) = 8.6
    c: DistanceY(g0,g5) = 10
    c: DistanceX(g7,g0) = 8
    c: DistanceY(g7,g6) = 24
    c: DistanceX(g6,g7) = 0
    c: Diameter(g7) = 5.6
    c: Equal(g7,g6)
    c: DistanceY(g7) = 23
    c: Coincident(g8,g9)
    c: Coincident(g10,g8)
    c: Horizontal(g8)
    c: Vertical(g9)
    c: Vertical(g10)
    c: DistanceX(g8) = 0.4
    c: PointOnObject(g8,g-1)
    c: DistanceX(g8,g0) = 0.4
    c: Coincident(g11,g12)
    c: Coincident(g12,g13)
    c: Coincident(g13,g14)
    c: Horizontal(g11)
    c: Horizontal(g13)
    c: Vertical(g12)
    c: Vertical(g14)
    c: DistanceY(g2,g11) = 27
    c: DistanceX(g11,g2) = 19
    c: Coincident(g14,g11)
    c: DistanceY(g14,g14) = 80
    c: DistanceX(g13,g13) = 114.6
    c: DistanceY(g2,g10) = 0.4
    c: Coincident(g10,g15)
    c: Horizontal(g15)
    c: Coincident(g15,g16)
    c: Vertical(g16)
    c: Coincident(g16,g17)
    c: Horizontal(g17)
    c: PointOnObject(g9,g2)
    c: DistanceX(g16,g11) = 0
    c: DistanceY(g16,g11) = 0.4
    c: DistanceX(g11,g17) = 20
    c: Coincident(g17,g18)
    c: Vertical(g18)
    c: Coincident(g18,g19)
    c: Coincident(g19,g9)
    c: Horizontal(g19)
FEATURE [PartDesign::Pad] Pad
  Direction = (0,0,1)
  Length = 10
  Length2 = 10
  Profile = -> Sketch
  ReferenceAxis = -> Sketch [N_Axis]
  Refine = true
  Suppressed = false
  Type = 0
FEATURE [Sketcher::SketchObject] Sketch001
  ArcFitTolerance = 1e-06
  AttachmentSupport = -> [Pad]
  FullyConstrained = true
  MakeInternals = false
  MapMode = 5
  Placement = pos=(0,0,10) rot=(0,0,1;0rad)
  expr: Constraints[11] = Sketch.Constraints[11]
  expr: Constraints[12] = Sketch.Constraints[12]
  expr: Constraints[13] = Sketch.Constraints[13]
  expr: Constraints[15] = Sketch.Constraints[15]
  expr: Constraints[16] = Sketch.Constraints[16]
  expr: Constraints[17] = Sketch.Constraints[17]
  expr: Constraints[18] = Sketch.Constraints[18]
  expr: Constraints[19] = Sketch.Constraints[19]
  expr: Constraints[20] = Sketch.Constraints[20]
  expr: Constraints[22] = Sketch.Constraints[22]
  expr: Constraints[31] = Sketch.Constraints[28]
  expr: Constraints[34] = Sketch.Constraints[30]
  expr: Constraints[8] = Sketch.Constraints[8]
  expr: Constraints[9] = Sketch.Constraints[9]
  sketch-geometry (14):
    g0: LineSegment [constr] StartX=0 StartY=0 StartZ=0 EndX=178 EndY=0 EndZ=0
    g1: LineSegment [constr] StartX=178 StartY=0 StartZ=0 EndX=178 EndY=70 EndZ=0
    g2: LineSegment [constr] StartX=178 StartY=70 StartZ=0 EndX=0 EndY=70 EndZ=0
    g3: LineSegment [constr] StartX=0 StartY=70 StartZ=0 EndX=0 EndY=0 EndZ=0
    g4: Circle [constr] CenterX=15 CenterY=60 CenterZ=0 NormalX=0 NormalY=0 NormalZ=1 AngleXU=0 Radius=4.3
    g5: Circle [constr] CenterX=15 CenterY=10 CenterZ=0 NormalX=0 NormalY=0 NormalZ=1 AngleXU=0 Radius=4.3
    g6: Circle [constr] CenterX=170 CenterY=47 CenterZ=0 NormalX=0 NormalY=0 NormalZ=1 AngleXU=0 Radius=2.8
    g7: Circle [constr] CenterX=170 CenterY=23 CenterZ=0 NormalX=0 NormalY=0 NormalZ=1 AngleXU=0 Radius=2.8
    g8: LineSegment [constr] StartX=0.4 StartY=0 StartZ=0 EndX=177.6 EndY=0 EndZ=0
    g9: LineSegment [constr] StartX=177.6 StartY=0 StartZ=0 EndX=177.6 EndY=70 EndZ=0
    g10: LineSegment [constr] StartX=177.6 StartY=70 StartZ=0 EndX=0.4 EndY=70 EndZ=0
    g11: LineSegment [constr] StartX=0.4 StartY=70 StartZ=0 EndX=0.4 EndY=0 EndZ=0
    g12: Circle CenterX=170 CenterY=47 CenterZ=0 NormalX=0 NormalY=0 NormalZ=1 AngleXU=0 Radius=4.5
    g13: Circle CenterX=170 CenterY=23 CenterZ=0 NormalX=0 NormalY=0 NormalZ=1 AngleXU=0 Radius=4.5
  constraints (39):
    c: Coincident(g0,g1)
    c: Coincident(g1,g2)
    c: Coincident(g2,g3)
    c: Coincident(g3,g0)
    c: Horizontal(g0)
    c: Horizontal(g2)
    c: Vertical(g1)
    c: Vertical(g3)
    c: Distance(g1,g3) = 178
    c: Distance(g0,g2) = 70
    c: Coincident(g0,g-1)
    c: DistanceX(g5) = 15
    c: DistanceX(g5,g4) = 0
    c: DistanceY(g5,g4) = 50
    c: Equal(g5,g4)
    c: Diameter(g5) = 8.6
    c: DistanceY(g0,g5) = 10
    c: DistanceX(g7,g0) = 8
    c: DistanceY(g7,g6) = 24
    c: DistanceX(g6,g7) = 0
    c: Diameter(g7) = 5.6
    c: Equal(g7,g6)
    c: DistanceY(g7) = 23
    c: Coincident(g8,g9)
    c: Coincident(g9,g10)
    c: Coincident(g10,g11)
    c: Coincident(g11,g8)
    c: Horizontal(g8)
    c: Horizontal(g10)
    c: Vertical(g9)
    c: Vertical(g11)
    c: DistanceX(g8) = 0.4
    c: PointOnObject(g8,g-1)
    c: PointOnObject(g10,g2)
    c: DistanceX(g8,g0) = 0.4
    c: Coincident(g12,g6)
    c: Coincident(g13,g7)
    c: Diameter(g13) = 9
    c: Equal(g13,g12)
FEATURE [PartDesign::Pocket] Pocket
  BaseFeature = -> Pad
  Direction = (0,0,-1)
  Length = 5
  Length2 = 5
  Profile = -> Sketch001
  ReferenceAxis = -> Sketch001 [N_Axis]
  Refine = true
  Suppressed = false
  Type = 0
FEATURE [PartDesign::Fillet] Fillet
  Base = -> Pocket [Edge30]
  BaseFeature = -> Pocket
  Radius = 4
  Refine = true
  SupportTransform = false
  Suppressed = false
  UseAllEdges = false
FEATURE [Sketcher::SketchObject] Sketch002
  ArcFitTolerance = 1e-06
  AttachmentSupport = -> [Fillet]
  FullyConstrained = true
  MakeInternals = false
  MapMode = 5
  Placement = pos=(0,0,10) rot=(0,0,1;0rad)
  sketch-geometry (20):
    g0: LineSegment [constr] StartX=-19 StartY=96.6 StartZ=0 EndX=95.6 EndY=96.6 EndZ=0
    g1: LineSegment [constr] StartX=95.6 StartY=96.6 StartZ=0 EndX=95.6 EndY=176.6 EndZ=0
    g2: LineSegment [constr] StartX=95.6 StartY=176.6 StartZ=0 EndX=-19 EndY=176.6 EndZ=0
    g3: LineSegment [constr] StartX=-19 StartY=176.6 StartZ=0 EndX=-19 EndY=96.6 EndZ=0
    g4: LineSegment [constr] StartX=-19 StartY=96.6 StartZ=0 EndX=-19 EndY=71.6 EndZ=0
    g5: LineSegment [constr] StartX=-19 StartY=71.6 StartZ=0 EndX=-4 EndY=71.6 EndZ=0
    g6: LineSegment [constr] StartX=-4 StartY=71.6 StartZ=0 EndX=-4 EndY=96.6 EndZ=0
    g7: LineSegment [constr] StartX=11 StartY=96.6 StartZ=0 EndX=11 EndY=71.6 EndZ=0
    g8: LineSegment [constr] StartX=11 StartY=71.6 StartZ=0 EndX=36 EndY=71.6 EndZ=0
    g9: LineSegment [constr] StartX=36 StartY=71.6 StartZ=0 EndX=36 EndY=96.6 EndZ=0
    g10: LineSegment [constr] StartX=95.6 StartY=96.6 StartZ=0 EndX=95.6 EndY=71.6 EndZ=0
    g11: LineSegment [constr] StartX=95.6 StartY=71.6 StartZ=0 EndX=110.6 EndY=71.6 EndZ=0
    g12: LineSegment [constr] StartX=110.6 StartY=71.6 StartZ=0 EndX=110.6 EndY=96.6 EndZ=0
    g13: LineSegment [constr] StartX=110.6 StartY=96.6 StartZ=0 EndX=95.6 EndY=96.6 EndZ=0
    g14: LineSegment [constr] StartX=-19 StartY=96.6 StartZ=0 EndX=-4 EndY=71.6 EndZ=0
    g15: LineSegment [constr] StartX=11 StartY=96.6 StartZ=0 EndX=36 EndY=71.6 EndZ=0
    g16: LineSegment [constr] StartX=95.6 StartY=96.6 StartZ=0 EndX=110.6 EndY=71.6 EndZ=0
    g17: Circle CenterX=-11.5 CenterY=84.1 CenterZ=0 NormalX=0 NormalY=0 NormalZ=1 AngleXU=0 Radius=4.3
    g18: Circle CenterX=23.5 CenterY=84.1 CenterZ=0 NormalX=0 NormalY=0 NormalZ=1 AngleXU=0 Radius=4.3
    g19: Circle CenterX=103.1 CenterY=84.1 CenterZ=0 NormalX=0 NormalY=0 NormalZ=1 AngleXU=0 Radius=4.3
  constraints (54):
    c: Coincident(g0,g1)
    c: Coincident(g1,g2)
    c: Coincident(g2,g3)
    c: Coincident(g3,g0)
    c: Horizontal(g0)
    c: Horizontal(g2)
    c: Vertical(g1)
    c: Vertical(g3)
    c: Distance(g1,g3) = 114.6
    c: Distance(g0,g2) = 80
    c: DistanceY(g0) = 96.6
    c: DistanceX(g0) = -19
    c: Coincident(g0,g4)
    c: Vertical(g4)
    c: Coincident(g4,g5)
    c: Horizontal(g5)
    c: Coincident(g5,g6)
    c: PointOnObject(g6,g0)
    c: Vertical(g6)
    c: PointOnObject(g7,g0)
    c: Vertical(g7)
    c: Coincident(g7,g8)
    c: Horizontal(g8)
    c: Coincident(g8,g9)
    c: PointOnObject(g9,g0)
    c: Vertical(g9)
    c: Coincident(g0,g10)
    c: Vertical(g10)
    c: Coincident(g10,g11)
    c: Horizontal(g11)
    c: Coincident(g11,g12)
    c: Vertical(g12)
    c: Coincident(g12,g13)
    c: Coincident(g13,g10)
    c: Horizontal(g13)
    c: DistanceY(g4,g4) = 25
    c: Equal(g6,g7)
    c: Equal(g7,g10)
    c: DistanceX(g5,g5) = 15
    c: DistanceX(g8,g8) = 25
    c: DistanceX(g0,g7) = 30
    c: DistanceX(g11,g11) = 15
    c: Coincident(g14,g0)
    c: Coincident(g14,g5)
    c: Coincident(g15,g7)
    c: Coincident(g15,g8)
    c: Coincident(g16,g0)
    c: Coincident(g16,g11)
    c: Diameter(g17) = 8.6
    c: Symmetric(g14,g14,g17)
    c: Symmetric(g15,g15,g18)
    c: Symmetric(g16,g16,g19)
    c: Equal(g19,g18)
    c: Equal(g18,g17)
FEATURE [PartDesign::Pocket] Pocket001
  BaseFeature = -> Fillet
  Direction = (0,0,-1)
  Length = 5
  Length2 = 5
  Profile = -> Sketch002
  ReferenceAxis = -> Sketch002 [N_Axis]
  Refine = true
  Suppressed = false
  Type = 1
FEATURE [PartDesign::Body] Body  label="sway_motor_mount_rear_plate"
  AllowCompound = false
  Group = -> [Sketch,Pad,Sketch001,Pocket,Fillet,Sketch002,Pocket001]
  Origin = -> Origin
  Tip = -> Pocket001
---- part sway_motor_mount_side.FCStd = doc fcstd_2a5d6e7b9529 (120205 chars; too large to inline — full recipe in that document) ----
---- part sway_motor_mount_top.FCStd = doc fcstd_c6dfb4d4f10d ----
FCSTD DOCUMENT  (FreeCAD 1.0R39109 (Git))
Label: sway_motor_mount_top
License: All rights reserved
LicenseURL: https://en.wikipedia.org/wiki/All_rights_reserved
objects: Sketcher::SketchObject×4, PartDesign::Pocket×3, PartDesign::Fillet×3, PartDesign::Pad×1, PartDesign::Groove×1, PartDesign::Body×1
note: 33 computed .brp shape members not serialized (recipe doc carries the construction recipe); baked Part::Feature solids carry a one-line shape summary decoded from their .brp

FEATURE [Sketcher::SketchObject] Sketch
  ArcFitTolerance = 1e-06
  AttachmentSupport = -> [XZ_Plane]
  FullyConstrained = true
  MakeInternals = false
  MapMode = 5
  Placement = pos=(0,0,0) rot=(1,0,0;1.5708rad)
  sketch-geometry (31):
    g0: LineSegment [constr] StartX=-66.2 StartY=5 StartZ=0 EndX=-66.2 EndY=-5 EndZ=0
    g1: LineSegment [constr] StartX=-66.2 StartY=-5 StartZ=0 EndX=-40 EndY=-5 EndZ=0
    g2: LineSegment [constr] StartX=-40 StartY=-5 StartZ=0 EndX=-40 EndY=5 EndZ=0
    g3: LineSegment [constr] StartX=-40 StartY=5 StartZ=0 EndX=-66.2 EndY=5 EndZ=0
    g4: LineSegment [constr] StartX=40 StartY=5 StartZ=0 EndX=40 EndY=-5 EndZ=0
    g5: LineSegment [constr] StartX=40 StartY=-5 StartZ=0 EndX=66.2 EndY=-5 EndZ=0
    g6: LineSegment [constr] StartX=66.2 StartY=-5 StartZ=0 EndX=66.2 EndY=5 EndZ=0
    g7: LineSegment [constr] StartX=66.2 StartY=5 StartZ=0 EndX=40 EndY=5 EndZ=0
    g8: LineSegment [constr] StartX=-40 StartY=-5 StartZ=0 EndX=0 EndY=0 EndZ=0
    g9: LineSegment [constr] StartX=0 StartY=0 StartZ=0 EndX=40 EndY=-5 EndZ=0
    g10: LineSegment [constr] StartX=-40 StartY=60 StartZ=0 EndX=-40 EndY=-20 EndZ=0
    g11: LineSegment [constr] StartX=-40 StartY=-20 StartZ=0 EndX=40 EndY=-20 EndZ=0
    g12: LineSegment [constr] StartX=40 StartY=-20 StartZ=0 EndX=40 EndY=60 EndZ=0
    g13: LineSegment [constr] StartX=40 StartY=60 StartZ=0 EndX=-40 EndY=60 EndZ=0
    g14: ArcOfCircle [constr] CenterX=-40 CenterY=-20 CenterZ=0 NormalX=0 NormalY=0 NormalZ=1 AngleXU=0 Radius=14 StartAngle=0 EndAngle=1.5708
    g15: ArcOfCircle [constr] CenterX=-40 CenterY=60 CenterZ=0 NormalX=0 NormalY=0 NormalZ=1 AngleXU=0 Radius=14 StartAngle=4.71239 EndAngle=6.28319
    g16: ArcOfCircle [constr] CenterX=40 CenterY=-20 CenterZ=0 NormalX=0 NormalY=0 NormalZ=1 AngleXU=0 Radius=14 StartAngle=1.5708 EndAngle=3.14159
    g17: ArcOfCircle [constr] CenterX=40 CenterY=60 CenterZ=0 NormalX=0 NormalY=0 NormalZ=1 AngleXU=0 Radius=14 StartAngle=3.14159 EndAngle=4.71239
    g18: ArcOfCircle CenterX=-40.4 CenterY=60.4 CenterZ=0 NormalX=0 NormalY=0 NormalZ=1 AngleXU=0 Radius=14 StartAngle=4.71239 EndAngle=6.28319
    g19: ArcOfCircle CenterX=40.4 CenterY=60.4 CenterZ=0 NormalX=0 NormalY=0 NormalZ=1 AngleXU=0 Radius=14 StartAngle=3.14159 EndAngle=4.71239
    g20: LineSegment StartX=-40.4 StartY=5.4 StartZ=0 EndX=-65.4 EndY=5.4 EndZ=0
    g21: LineSegment StartX=-65.4 StartY=5.4 StartZ=0 EndX=-65.4 EndY=15.4 EndZ=0
    g22: LineSegment StartX=-65.4 StartY=15.4 StartZ=0 EndX=-34.5532 EndY=65.4 EndZ=0
    g23: LineSegment StartX=-34.5532 StartY=65.4 StartZ=0 EndX=34.5532 EndY=65.4 EndZ=0
    g24: LineSegment StartX=34.5532 StartY=65.4 StartZ=0 EndX=65.4 EndY=15.4 EndZ=0
    g25: LineSegment StartX=65.4 StartY=15.4 StartZ=0 EndX=65.4 EndY=5.4 EndZ=0
    g26: LineSegment StartX=65.4 StartY=5.4 StartZ=0 EndX=40.4 EndY=5.4 EndZ=0
    g27: LineSegment StartX=40.4 StartY=5.4 StartZ=0 EndX=40.4 EndY=46.4 EndZ=0
    g28: LineSegment StartX=-26.4 StartY=60.4 StartZ=0 EndX=26.4 EndY=60.4 EndZ=0
    g29: LineSegment StartX=-40.4 StartY=46.4 StartZ=0 EndX=-40.4 EndY=5.4 EndZ=0
    g30: LineSegment [constr] StartX=-44.6553 StartY=49.0253 StartZ=0 EndX=-40.4 EndY=46.4 EndZ=0
  constraints (97):
    c: Coincident(g0,g1)
    c: Coincident(g1,g2)
    c: Coincident(g2,g3)
    c: Coincident(g3,g0)
    c: Vertical(g0)
    c: Vertical(g2)
    c: Horizontal(g1)
    c: Horizontal(g3)
    c: Coincident(g4,g5)
    c: Coincident(g5,g6)
    c: Coincident(g6,g7)
    c: Coincident(g7,g4)
    c: Vertical(g4)
    c: Vertical(g6)
    c: Horizontal(g5)
    c: Horizontal(g7)
    c: Equal(g2,g4)
    c: DistanceY(g0,g0) = 10
    c: DistanceX(g2,g4) = 80
    c: DistanceY(g2,g4) = 0
    c: Coincident(g8,g1)
    c: Coincident(g8,g-1)
    c: Coincident(g9,g8)
    c: Coincident(g9,g4)
    c: Equal(g9,g8)
    c: Coincident(g10,g11)
    c: Coincident(g11,g12)
    c: Coincident(g12,g13)
    c: Coincident(g13,g10)
    c: Vertical(g10)
    c: Vertical(g12)
    c: Horizontal(g11)
    c: Horizontal(g13)
    c: PointOnObject(g2,g10)
    c: PointOnObject(g4,g12)
    c: Equal(g13,g10)
    c: DistanceY(g2,g10) = 55
    c: DistanceY(g2) = 5
    c: Coincident(g14,g10)
    c: PointOnObject(g14,g10)
    c: PointOnObject(g14,g11)
    c: Diameter(g14) = 28
    c: Coincident(g15,g10)
    c: PointOnObject(g15,g13)
    c: PointOnObject(g15,g10)
    c: Coincident(g16,g11)
    c: PointOnObject(g16,g11)
    c: PointOnObject(g16,g12)
    c: Coincident(g17,g12)
    c: PointOnObject(g17,g13)
    c: PointOnObject(g17,g12)
    c: Equal(g14,g16)
    c: Equal(g16,g17)
    c: Equal(g17,g15)
    c: Horizontal(g20)
    c: Coincident(g20,g21)
    c: Vertical(g21)
    c: Coincident(g21,g22)
    c: Coincident(g22,g23)
    c: Horizontal(g23)
    c: Coincident(g23,g24)
    c: Coincident(g24,g25)
    c: Vertical(g25)
    c: Coincident(g25,g26)
    c: Horizontal(g26)
    c: Coincident(g26,g27)
    c: Coincident(g27,g19)
    c: Vertical(g27)
    c: Coincident(g28,g18)
    c: Coincident(g28,g19)
    c: Horizontal(g28)
    c: Coincident(g29,g18)
    c: Coincident(g29,g20)
    c: Vertical(g29)
    c: DistanceY(g0,g20) = 0.4
    c: DistanceX(g20,g2) = 0.4
    c: Perpendicular(g18,g29)
    c: DistanceY(g15,g18) = 0.4
    c: Perpendicular(g18,g28)
    c: DistanceY(g18,g22) = 5
    c: DistanceY(g20,g21) = 10
    c: Equal(g21,g25)
    c: Equal(g22,g24)
    c: DistanceX(g4,g26) = 0.4
    c: DistanceY(g4,g26) = 0.4
    c: Equal(g27,g29)
    c: Perpendicular(g19,g27)
    c: Perpendicular(g19,g28)
    c: DistanceY(g15,g18) = 0.4
    c: Equal(g3,g7)
    c: DistanceX(g1,g1) = 26.2
    c: DistanceX(g20,g20) = 25
    c: Equal(g26,g20)
    c: PointOnObject(g30,g22)
    c: Coincident(g30,g18)
    c: Perpendicular(g22,g30)
    c: Distance(g30) = 5
FEATURE [PartDesign::Pad] Pad
  Direction = (0,-1,2e-16)
  Length = 15
  Length2 = 10
  Placement = pos=(0,0,0) rot=(1,0,0;1.5708rad)
  Profile = -> Sketch
  ReferenceAxis = -> Sketch [N_Axis]
  Refine = true
  Suppressed = false
  Type = 0
FEATURE [Sketcher::SketchObject] Sketch001
  ArcFitTolerance = 1e-06
  AttachmentSupport = -> [Pad]
  FullyConstrained = true
  MakeInternals = false
  MapMode = 5
  Placement = pos=(0,2.4e-15,5.4) rot=(1,0,0;3.14159rad)
  sketch-geometry (14):
    g0: LineSegment [constr] StartX=-65.4 StartY=1.8e-15 StartZ=0 EndX=-40.4 EndY=1.8e-15 EndZ=0
    g1: LineSegment [constr] StartX=-40.4 StartY=1.8e-15 StartZ=0 EndX=-40.4 EndY=15 EndZ=0
    g2: LineSegment [constr] StartX=-40.4 StartY=15 StartZ=0 EndX=-65.4 EndY=15 EndZ=0
    g3: LineSegment [constr] StartX=-65.4 StartY=15 StartZ=0 EndX=-65.4 EndY=1.8e-15 EndZ=0
    g4: LineSegment [constr] StartX=65.4 StartY=0 StartZ=0 EndX=65.4 EndY=15 EndZ=0
    g5: LineSegment [constr] StartX=65.4 StartY=15 StartZ=0 EndX=40.4 EndY=15 EndZ=0
    g6: LineSegment [constr] StartX=40.4 StartY=15 StartZ=0 EndX=40.4 EndY=0 EndZ=0
    g7: LineSegment [constr] StartX=40.4 StartY=0 StartZ=0 EndX=65.4 EndY=0 EndZ=0
    g8: LineSegment [constr] StartX=-65.4 StartY=15 StartZ=0 EndX=-40.4 EndY=3.6e-15 EndZ=0
    g9: LineSegment [constr] StartX=-65.4 StartY=1.8e-15 StartZ=0 EndX=-40.4 EndY=15 EndZ=0
    g10: LineSegment [constr] StartX=40.4 StartY=15 StartZ=0 EndX=65.4 EndY=3.6e-15 EndZ=0
    g11: LineSegment [constr] StartX=40.4 StartY=0 StartZ=0 EndX=65.4 EndY=15 EndZ=0
    g12: Circle CenterX=-52.9 CenterY=7.5 CenterZ=0 NormalX=0 NormalY=0 NormalZ=1 AngleXU=0 Radius=4.3
    g13: Circle CenterX=52.9 CenterY=7.5 CenterZ=0 NormalX=0 NormalY=0 NormalZ=1 AngleXU=0 Radius=4.3
  constraints (36):
    c: Coincident(g0,g1)
    c: Coincident(g1,g2)
    c: Coincident(g2,g3)
    c: Coincident(g3,g0)
    c: Horizontal(g0)
    c: Horizontal(g2)
    c: Vertical(g1)
    c: Vertical(g3)
    c: Distance(g1,g3) = 25
    c: Distance(g0,g2) = 15
    c: PointOnObject(g0,g-1)
    c: DistanceX(g0) = -40.4
    c: Coincident(g4,g5)
    c: Coincident(g5,g6)
    c: Coincident(g6,g7)
    c: Coincident(g7,g4)
    c: Vertical(g4)
    c: Vertical(g6)
    c: Horizontal(g5)
    c: Horizontal(g7)
    c: PointOnObject(g4,g-1)
    c: DistanceX(g6) = 40.4
    c: Coincident(g8,g2)
    c: Coincident(g8,g0)
    c: Coincident(g9,g0)
    c: Coincident(g9,g1)
    c: Coincident(g10,g5)
    c: Coincident(g10,g4)
    c: Coincident(g11,g6)
    c: Coincident(g11,g4)
    c: Diameter(g12) = 8.6
    c: Symmetric(g8,g8,g12)
    c: Symmetric(g11,g11,g13)
    c: Equal(g2,g5)
    c: Equal(g3,g4)
    c: Equal(g12,g13)
FEATURE [PartDesign::Pocket] Pocket
  BaseFeature = -> Pad
  Direction = (0,0,1)
  Length = 5
  Length2 = 5
  Placement = pos=(0,0,0) rot=(1,0,0;1.5708rad)
  Profile = -> Sketch001
  ReferenceAxis = -> Sketch001 [N_Axis]
  Refine = true
  Suppressed = false
  Type = 1
FEATURE [Sketcher::SketchObject] Sketch002
  ArcFitTolerance = 1e-06
  AttachmentOffset = pos=(0,0,-5) rot=(0,0,1;0rad)
  AttachmentSupport = -> [Pocket]
  FullyConstrained = true
  MakeInternals = false
  MapMode = 5
  Placement = pos=(0,2.4e-15,10.4) rot=(1,0,0;3.14159rad)
  expr: Constraints[11] = Sketch001.Constraints[11]
  expr: Constraints[21] = Sketch001.Constraints[21]
  expr: Constraints[30] = Sketch001.Constraints[30]
  expr: Constraints[8] = Sketch001.Constraints[8]
  expr: Constraints[9] = Sketch001.Constraints[9]
  sketch-geometry (16):
    g0: LineSegment [constr] StartX=-65.4 StartY=0 StartZ=0 EndX=-40.4 EndY=0 EndZ=0
    g1: LineSegment [constr] StartX=-40.4 StartY=0 StartZ=0 EndX=-40.4 EndY=15 EndZ=0
    g2: LineSegment [constr] StartX=-40.4 StartY=15 StartZ=0 EndX=-65.4 EndY=15 EndZ=0
    g3: LineSegment [constr] StartX=-65.4 StartY=15 StartZ=0 EndX=-65.4 EndY=0 EndZ=0
    g4: LineSegment [constr] StartX=65.4 StartY=0 StartZ=0 EndX=65.4 EndY=15 EndZ=0
    g5: LineSegment [constr] StartX=65.4 StartY=15 StartZ=0 EndX=40.4 EndY=15 EndZ=0
    g6: LineSegment [constr] StartX=40.4 StartY=15 StartZ=0 EndX=40.4 EndY=0 EndZ=0
    g7: LineSegment [constr] StartX=40.4 StartY=0 StartZ=0 EndX=65.4 EndY=0 EndZ=0
    g8: LineSegment [constr] StartX=-65.4 StartY=15 StartZ=0 EndX=-40.4 EndY=3.6e-15 EndZ=0
    g9: LineSegment [constr] StartX=-65.4 StartY=0 StartZ=0 EndX=-40.4 EndY=15 EndZ=0
    g10: LineSegment [constr] StartX=40.4 StartY=15 StartZ=0 EndX=65.4 EndY=3.6e-15 EndZ=0
    g11: LineSegment [constr] StartX=40.4 StartY=0 StartZ=0 EndX=65.4 EndY=15 EndZ=0
    g12: Circle [constr] CenterX=-52.9 CenterY=7.5 CenterZ=0 NormalX=0 NormalY=0 NormalZ=1 AngleXU=0 Radius=4.3
    g13: Circle [constr] CenterX=52.9 CenterY=7.5 CenterZ=0 NormalX=0 NormalY=0 NormalZ=1 AngleXU=0 Radius=4.3
    g14: Circle CenterX=-52.9 CenterY=7.5 CenterZ=0 NormalX=0 NormalY=0 NormalZ=1 AngleXU=0 Radius=6.75
    g15: Circle CenterX=52.9 CenterY=7.5 CenterZ=0 NormalX=0 NormalY=0 NormalZ=1 AngleXU=0 Radius=6.75
  constraints (40):
    c: Coincident(g0,g1)
    c: Coincident(g1,g2)
    c: Coincident(g2,g3)
    c: Coincident(g3,g0)
    c: Horizontal(g0)
    c: Horizontal(g2)
    c: Vertical(g1)
    c: Vertical(g3)
    c: Distance(g1,g3) = 25
    c: Distance(g0,g2) = 15
    c: PointOnObject(g0,g-1)
    c: DistanceX(g0) = -40.4
    c: Coincident(g4,g5)
    c: Coincident(g5,g6)
    c: Coincident(g6,g7)
    c: Coincident(g7,g4)
    c: Vertical(g4)
    c: Vertical(g6)
    c: Horizontal(g5)
    c: Horizontal(g7)
    c: PointOnObject(g4,g-1)
    c: DistanceX(g6) = 40.4
    c: Coincident(g8,g2)
    c: Coincident(g8,g0)
    c: Coincident(g9,g0)
    c: Coincident(g9,g1)
    c: Coincident(g10,g5)
    c: Coincident(g10,g4)
    c: Coincident(g11,g6)
    c: Coincident(g11,g4)
    c: Diameter(g12) = 8.6
    c: Symmetric(g8,g8,g12)
    c: Symmetric(g11,g11,g13)
    c: Equal(g13,g12)
    c: Coincident(g14,g12)
    c: Coincident(g15,g13)
    c: Equal(g14,g15)
    c: Diameter(g14) = 13.5
    c: Equal(g4,g3)
    c: Equal(g5,g2)
FEATURE [PartDesign::Pocket] Pocket001
  BaseFeature = -> Pocket
  Direction = (0,0,1)
  Length = 5
  Length2 = 5
  Placement = pos=(0,0,0) rot=(1,0,0;1.5708rad)
  Profile = -> Sketch002
  ReferenceAxis = -> Sketch002 [N_Axis]
  Refine = true
  Suppressed = false
  Type = 1
FEATURE [PartDesign::Fillet] Fillet
  Base = -> Pocket001 [Edge27,Edge18,Edge23,Edge14]
  BaseFeature = -> Pocket001
  Placement = pos=(0,0,0) rot=(1,0,0;1.5708rad)
  Radius = 4
  Refine = true
  SupportTransform = false
  Suppressed = false
  UseAllEdges = false
FEATURE [PartDesign::Fillet] Fillet001
  Base = -> Fillet [Edge30,Edge23]
  BaseFeature = -> Fillet
  Placement = pos=(0,0,0) rot=(1,0,0;1.5708rad)
  Radius = 18
  Refine = true
  SupportTransform = false
  Suppressed = false
  UseAllEdges = false
FEATURE [Sketcher::SketchObject] Sketch003
  ArcFitTolerance = 1e-06
  AttachmentSupport = -> [Fillet001]
  FullyConstrained = true
  MakeInternals = false
  MapMode = 5
  Placement = pos=(0,-15,0) rot=(1,0,0;1.5708rad)
  sketch-geometry (4):
    g0: ArcOfCircle CenterX=-7 CenterY=65.4 CenterZ=0 NormalX=0 NormalY=0 NormalZ=1 AngleXU=0 Radius=3 StartAngle=3.14159 EndAngle=4.71239
    g1: ArcOfCircle CenterX=7 CenterY=65.4 CenterZ=0 NormalX=0 NormalY=0 NormalZ=1 AngleXU=0 Radius=3 StartAngle=4.71239 EndAngle=6.28319
    g2: LineSegment StartX=-7 StartY=62.4 StartZ=0 EndX=7 EndY=62.4 EndZ=0
    g3: LineSegment StartX=-10 StartY=65.4 StartZ=0 EndX=10 EndY=65.4 EndZ=0
  constraints (12):
    c: Coincident(g3,g0)
    c: Coincident(g3,g1)
    c: Horizontal(g3)
    c: Horizontal(g2)
    c: PointOnObject(g1,g3)
    c: PointOnObject(g0,g3)
    c: Tangent(g2,g1) = -1.5708
    c: Tangent(g2,g0) = -1.5708
    c: DistanceX(g3,g3) = 20
    c: DistanceX(g0) = -10
    c: DistanceY(g0) = 65.4
    c: DistanceY(g0,g0) = 3
FEATURE [PartDesign::Pocket] Pocket002
  BaseFeature = -> Fillet001
  Direction = (0,1,-2e-16)
  Length = 3
  Length2 = 5
  Placement = pos=(0,0,0) rot=(1,0,0;1.5708rad)
  Profile = -> Sketch003
  ReferenceAxis = -> Sketch003 [N_Axis]
  Refine = true
  Suppressed = false
  Type = 0
FEATURE [PartDesign::Groove] Groove
  Angle = 90
  Angle2 = 60
  Axis = (1,0,0)
  Base = (-10,-12,65.4)
  BaseFeature = -> Pocket002
  Placement = pos=(0,0,0) rot=(1,0,0;1.5708rad)
  Profile = -> Pocket002 [Face21]
  ReferenceAxis = -> Pocket002 [Edge27]
  Refine = true
  Suppressed = false
  Type = 0
FEATURE [PartDesign::Fillet] Fillet002
  Base = -> Groove [Edge28]
  BaseFeature = -> Groove
  Placement = pos=(0,0,0) rot=(1,0,0;1.5708rad)
  Radius = 3
  Refine = true
  SupportTransform = false
  Suppressed = false
  UseAllEdges = false
FEATURE [PartDesign::Body] Body  label="sway_motor_mount_top"
  AllowCompound = false
  Group = -> [Sketch,Pad,Sketch001,Pocket,Sketch002,Pocket001,Fillet,Fillet001,Sketch003,Pocket002,Groove,Fillet002]
  Origin = -> Origin
  Tip = -> Fillet002
